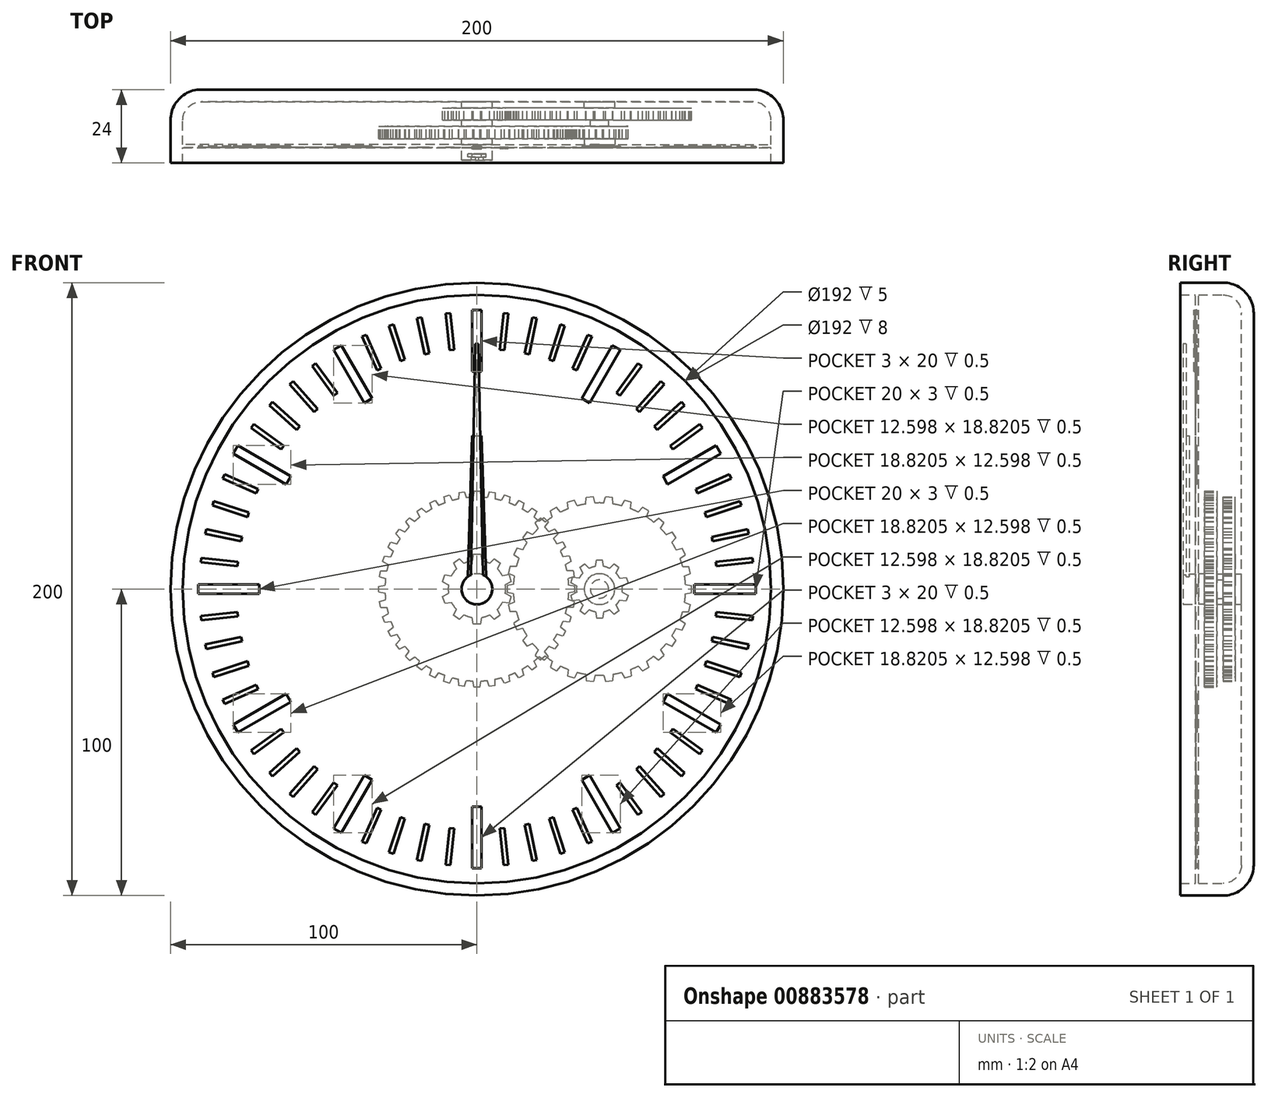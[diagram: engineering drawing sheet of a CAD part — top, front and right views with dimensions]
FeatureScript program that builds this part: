
annotation { "Feature Type Name" : "Feature", "Feature Type Description" : "" }
export const myFeature = defineFeature(function(context is Context, id is Id, definition is map)
    precondition{}
    {
        {
            var Q0;
            Q0=qCreatedBy(makeId("Front.planeOp"),FACE);
            var sketch = newSketch(context, id + "F0", { "sketchPlane" : qUnion([Q0])});
            skCircle(sketch, "E0", {"center": v(0, 0) * mm, "radius": 100 * mm});
            skSolve(sketch);
        }
        {
            var Q0;
            Q0 = qSketchRegion(id + "F0", true);
            extrude(context, id + "F1", {"entities" : qUnion([Q0]), "depth" : 24 * mm, "offsetDistance" : 25 * mm});
        }
        {
            var Q0;
            Q0=makeQuery(id+"F1.opExtrude","CAP_EDGE",EDGE,{"disambiguationData":[OSD([sQuery(id+"F0.wireOp",EDGE,"E0")])],"isStart":true});
            fillet(context, id + "F2", {"entities" : qUnion([Q0]), "radius" : 10 * mm, "tangentPropagation" : true, "allowEdgeOverflow" : false});
        }
        {
            var Q0;
            Q0=makeQuery(id+"F1.opExtrude","CAP_FACE",FACE,{"disambiguationData":[OSD([sQuery(id+"F0.wireOp",EDGE,"E0")])],"isStart":false});
            shell(context, id + "F3", {"entities" : qUnion([Q0]), "thickness" : 4 * mm});
        }
        {
            var Q0;
            {var subQ0=sQuery(id+"F0.wireOp",EDGE,"E0");Q0=makeQuery(id+"F3.opShell","OFFSET_FACE",FACE,{"disambiguationData":[OSD([subQ0]),TDD([makeQuery(id+"F1.opExtrude","CAP_FACE",FACE,{"disambiguationData":[OSD([subQ0])],"isStart":true})])]});}
            var sketch = newSketch(context, id + "F4", { "sketchPlane" : qUnion([Q0])});
            skCircle(sketch, "E1", {"center": v(0, 0) * mm, "radius": 5 * mm});
            skCircle(sketch, "E2", {"center": v(0, 0) * mm, "radius": 3 * mm});
            skCircle(sketch, "E3", {"center": v(40, 0) * mm, "radius": 5 * mm});
            skCircle(sketch, "E4", {"center": v(40, 0) * mm, "radius": 3 * mm});
            skSolve(sketch);
        }
        {
            var Q0;
            Q0 = qSketchRegion(id + "F4", true);
            extrude(context, id + "F5", {"entities" : qUnion([Q0]), "operationType" : NewBodyOperationType.ADD, "depth" : 2 * mm, "offsetDistance" : 25 * mm});
        }
        {
            var Q0;
            {var subQ0=sQuery(id+"F0.wireOp",EDGE,"E0");Q0=makeQuery(id+"F5.boolean.opBoolean","SPLIT",FACE,{"disambiguationData":[TD([makeQuery(id+"F5.opExtrude","SWEPT_FACE",FACE,{"disambiguationData":[OSD([sQuery(id+"F4.wireOp",EDGE,"E2")])]})])],"derivedFrom":makeQuery(id+"F3.opShell","OFFSET_FACE",FACE,{"disambiguationData":[OSD([subQ0]),TDD([makeQuery(id+"F1.opExtrude","CAP_FACE",FACE,{"disambiguationData":[OSD([subQ0])],"isStart":true})])]})});}
            extrude(context, id + "F6", {"entities" : qUnion([Q0]), "depth" : 19 * mm, "offsetDistance" : 25 * mm});
        }
        {
            var Q0;
            {var subQ0=sQuery(id+"F0.wireOp",EDGE,"E0");Q0=makeQuery(id+"F5.boolean.opBoolean","SPLIT",FACE,{"disambiguationData":[TD([makeQuery(id+"F5.opExtrude","SWEPT_FACE",FACE,{"disambiguationData":[OSD([sQuery(id+"F4.wireOp",EDGE,"E4")])]})])],"derivedFrom":makeQuery(id+"F3.opShell","OFFSET_FACE",FACE,{"disambiguationData":[OSD([subQ0]),TDD([makeQuery(id+"F1.opExtrude","CAP_FACE",FACE,{"disambiguationData":[OSD([subQ0])],"isStart":true})])]})});}
            extrude(context, id + "F7", {"entities" : qUnion([Q0]), "depth" : 8 * mm, "offsetDistance" : 25 * mm});
        }
        {
            var Q0;
            Q0=makeQuery(id+"F5.opExtrude","CAP_FACE",FACE,{"disambiguationData":[OSD([sQuery(id+"F4.wireOp",EDGE,"E1"),sQuery(id+"F4.wireOp",EDGE,"E2")])],"isStart":false});
            var sketch = newSketch(context, id + "F8", { "sketchPlane" : qUnion([Q0])});
            skCircle(sketch, "E5", {"center": v(0, 0) * mm, "radius": 9.38 * mm});
            skLineSegment(sketch, "E6", {"start": v(0, 11.38) * mm, "end": v(1.18, 11.38) * mm});
            skLineSegment(sketch, "E7", {"start": v(1.18, 11.38) * mm, "end": v(1.55, 9.25) * mm});
            skLineSegment(sketch, "E8.MirrorCS", {"start": v(0, 11.38) * mm, "end": v(-1.18, 11.38) * mm});
            skLineSegment(sketch, "E9.MirrorCS", {"start": v(-1.18, 11.38) * mm, "end": v(-1.55, 9.25) * mm});
            skLineSegment(sketch, "E10.1.0", {"start": v(-6.69, 9.2) * mm, "end": v(-5.73, 9.9) * mm});
            skLineSegment(sketch, "E10.1.1", {"start": v(-6.69, 9.2) * mm, "end": v(-7.64, 8.51) * mm});
            skLineSegment(sketch, "E10.1.2", {"start": v(-5.73, 9.9) * mm, "end": v(-4.18, 8.4) * mm});
            skLineSegment(sketch, "E10.1.3", {"start": v(-7.64, 8.51) * mm, "end": v(-6.7, 6.57) * mm});
            skLineSegment(sketch, "E10.2.0", {"start": v(-10.82, 3.52) * mm, "end": v(-10.45, 4.64) * mm});
            skLineSegment(sketch, "E10.2.1", {"start": v(-10.82, 3.52) * mm, "end": v(-11.18, 2.4) * mm});
            skLineSegment(sketch, "E10.2.2", {"start": v(-10.45, 4.64) * mm, "end": v(-8.31, 4.33) * mm});
            skLineSegment(sketch, "E10.2.3", {"start": v(-11.18, 2.4) * mm, "end": v(-9.27, 1.38) * mm});
            skLineSegment(sketch, "E11.3.3.0", {"start": v(-10.82, -3.52) * mm, "end": v(-10.45, -4.64) * mm});
            skLineSegment(sketch, "E11.6.3.0", {"start": v(-11.18, -2.4) * mm, "end": v(-9.27, -1.38) * mm});
            skLineSegment(sketch, "E11.8.3.0", {"start": v(-10.82, -3.52) * mm, "end": v(-11.18, -2.4) * mm});
            skLineSegment(sketch, "E11.9.3.0", {"start": v(-10.45, -4.64) * mm, "end": v(-8.31, -4.33) * mm});
            skLineSegment(sketch, "E11.3.4.0", {"start": v(-6.69, -9.2) * mm, "end": v(-5.73, -9.9) * mm});
            skLineSegment(sketch, "E11.6.4.0", {"start": v(-7.64, -8.51) * mm, "end": v(-6.7, -6.57) * mm});
            skLineSegment(sketch, "E11.8.4.0", {"start": v(-6.69, -9.2) * mm, "end": v(-7.64, -8.51) * mm});
            skLineSegment(sketch, "E11.9.4.0", {"start": v(-5.73, -9.9) * mm, "end": v(-4.18, -8.4) * mm});
            skLineSegment(sketch, "E11.3.5.0", {"start": v(0, -11.38) * mm, "end": v(1.18, -11.38) * mm});
            skLineSegment(sketch, "E11.6.5.0", {"start": v(-1.18, -11.38) * mm, "end": v(-1.55, -9.25) * mm});
            skLineSegment(sketch, "E11.8.5.0", {"start": v(0, -11.38) * mm, "end": v(-1.18, -11.38) * mm});
            skLineSegment(sketch, "E11.9.5.0", {"start": v(1.18, -11.38) * mm, "end": v(1.55, -9.25) * mm});
            skLineSegment(sketch, "E11.3.6.0", {"start": v(6.69, -9.2) * mm, "end": v(7.64, -8.51) * mm});
            skLineSegment(sketch, "E11.6.6.0", {"start": v(5.73, -9.9) * mm, "end": v(4.18, -8.4) * mm});
            skLineSegment(sketch, "E11.8.6.0", {"start": v(6.69, -9.2) * mm, "end": v(5.73, -9.9) * mm});
            skLineSegment(sketch, "E11.9.6.0", {"start": v(7.64, -8.51) * mm, "end": v(6.7, -6.57) * mm});
            skLineSegment(sketch, "E11.3.7.0", {"start": v(10.82, -3.52) * mm, "end": v(11.18, -2.4) * mm});
            skLineSegment(sketch, "E11.6.7.0", {"start": v(10.45, -4.64) * mm, "end": v(8.31, -4.33) * mm});
            skLineSegment(sketch, "E11.8.7.0", {"start": v(10.82, -3.52) * mm, "end": v(10.45, -4.64) * mm});
            skLineSegment(sketch, "E11.9.7.0", {"start": v(11.18, -2.4) * mm, "end": v(9.27, -1.38) * mm});
            skLineSegment(sketch, "E11.3.8.0", {"start": v(10.82, 3.52) * mm, "end": v(10.45, 4.64) * mm});
            skLineSegment(sketch, "E11.6.8.0", {"start": v(11.18, 2.4) * mm, "end": v(9.27, 1.38) * mm});
            skLineSegment(sketch, "E11.8.8.0", {"start": v(10.82, 3.52) * mm, "end": v(11.18, 2.4) * mm});
            skLineSegment(sketch, "E11.9.8.0", {"start": v(10.45, 4.64) * mm, "end": v(8.31, 4.33) * mm});
            skLineSegment(sketch, "E11.3.9.0", {"start": v(6.69, 9.2) * mm, "end": v(5.73, 9.9) * mm});
            skLineSegment(sketch, "E11.6.9.0", {"start": v(7.64, 8.51) * mm, "end": v(6.7, 6.57) * mm});
            skLineSegment(sketch, "E11.8.9.0", {"start": v(6.69, 9.2) * mm, "end": v(7.64, 8.51) * mm});
            skLineSegment(sketch, "E11.9.9.0", {"start": v(5.73, 9.9) * mm, "end": v(4.18, 8.4) * mm});
            skSolve(sketch);
        }
        {
            var Q0;
            Q0 = qSketchRegion(id + "F8", true);
            extrude(context, id + "F9", {"entities" : qUnion([Q0]), "operationType" : NewBodyOperationType.ADD, "depth" : 4 * mm, "offsetDistance" : 25 * mm});
        }
        {
            var Q0;
            Q0=makeQuery(id+"F5.opExtrude","CAP_FACE",FACE,{"disambiguationData":[OSD([sQuery(id+"F4.wireOp",EDGE,"E3"),sQuery(id+"F4.wireOp",EDGE,"E4")])],"isStart":false});
            var sketch = newSketch(context, id + "F10", { "sketchPlane" : qUnion([Q0])});
            skCircle(sketch, "E12", {"center": v(40, 0) * mm, "radius": 28.12 * mm});
            skLineSegment(sketch, "E13", {"start": v(11.92, 1.53) * mm, "end": v(9.9, 1.18) * mm});
            skLineSegment(sketch, "E14", {"start": v(9.9, 1.18) * mm, "end": v(9.9, 0) * mm});
            skLineSegment(sketch, "E15.MirrorCS", {"start": v(9.9, -1.18) * mm, "end": v(9.9, 0) * mm});
            skLineSegment(sketch, "E16.MirrorCS", {"start": v(11.92, -1.53) * mm, "end": v(9.9, -1.18) * mm});
            skLineSegment(sketch, "E17.1.0", {"start": v(12.21, -4.34) * mm, "end": v(10.31, -5.1) * mm});
            skLineSegment(sketch, "E17.1.1", {"start": v(10.31, -5.1) * mm, "end": v(10.56, -6.26) * mm});
            skLineSegment(sketch, "E17.1.2", {"start": v(10.8, -7.41) * mm, "end": v(10.56, -6.26) * mm});
            skLineSegment(sketch, "E17.1.3", {"start": v(12.85, -7.34) * mm, "end": v(10.8, -7.41) * mm});
            skLineSegment(sketch, "E17.2.0", {"start": v(13.72, -10.02) * mm, "end": v(12.02, -11.17) * mm});
            skLineSegment(sketch, "E17.2.1", {"start": v(12.02, -11.17) * mm, "end": v(12.5, -12.24) * mm});
            skLineSegment(sketch, "E17.2.2", {"start": v(12.98, -13.32) * mm, "end": v(12.5, -12.24) * mm});
            skLineSegment(sketch, "E17.2.3", {"start": v(14.97, -12.82) * mm, "end": v(12.98, -13.32) * mm});
            skLineSegment(sketch, "E18.2.3.0", {"start": v(16.38, -15.27) * mm, "end": v(14.95, -16.74) * mm});
            skLineSegment(sketch, "E18.3.3.0", {"start": v(14.95, -16.74) * mm, "end": v(15.65, -17.7) * mm});
            skLineSegment(sketch, "E18.6.3.0", {"start": v(16.34, -18.65) * mm, "end": v(15.65, -17.7) * mm});
            skLineSegment(sketch, "E18.9.3.0", {"start": v(18.18, -17.75) * mm, "end": v(16.34, -18.65) * mm});
            skLineSegment(sketch, "E18.2.4.0", {"start": v(20.07, -19.84) * mm, "end": v(18.98, -21.58) * mm});
            skLineSegment(sketch, "E18.3.4.0", {"start": v(18.98, -21.58) * mm, "end": v(19.86, -22.37) * mm});
            skLineSegment(sketch, "E18.6.4.0", {"start": v(20.73, -23.16) * mm, "end": v(19.86, -22.37) * mm});
            skLineSegment(sketch, "E18.9.4.0", {"start": v(22.35, -21.9) * mm, "end": v(20.73, -23.16) * mm});
            skLineSegment(sketch, "E18.2.5.0", {"start": v(24.63, -23.55) * mm, "end": v(23.93, -25.48) * mm});
            skLineSegment(sketch, "E18.3.5.0", {"start": v(23.93, -25.48) * mm, "end": v(24.95, -26.07) * mm});
            skLineSegment(sketch, "E18.6.5.0", {"start": v(25.97, -26.66) * mm, "end": v(24.95, -26.07) * mm});
            skLineSegment(sketch, "E18.9.5.0", {"start": v(27.29, -25.09) * mm, "end": v(25.97, -26.66) * mm});
            skLineSegment(sketch, "E18.2.6.0", {"start": v(29.86, -26.23) * mm, "end": v(29.58, -28.26) * mm});
            skLineSegment(sketch, "E18.3.6.0", {"start": v(29.58, -28.26) * mm, "end": v(30.7, -28.63) * mm});
            skLineSegment(sketch, "E18.6.6.0", {"start": v(31.82, -29) * mm, "end": v(30.7, -28.63) * mm});
            skLineSegment(sketch, "E18.9.6.0", {"start": v(32.78, -27.18) * mm, "end": v(31.82, -29) * mm});
            skLineSegment(sketch, "E18.2.7.0", {"start": v(35.54, -27.77) * mm, "end": v(35.68, -29.81) * mm});
            skLineSegment(sketch, "E18.3.7.0", {"start": v(35.68, -29.81) * mm, "end": v(36.85, -29.94) * mm});
            skLineSegment(sketch, "E18.6.7.0", {"start": v(38.03, -30.06) * mm, "end": v(36.85, -29.94) * mm});
            skLineSegment(sketch, "E18.9.7.0", {"start": v(38.6, -28.09) * mm, "end": v(38.03, -30.06) * mm});
            skLineSegment(sketch, "E18.2.8.0", {"start": v(41.4, -28.09) * mm, "end": v(41.97, -30.06) * mm});
            skLineSegment(sketch, "E18.3.8.0", {"start": v(41.97, -30.06) * mm, "end": v(43.15, -29.94) * mm});
            skLineSegment(sketch, "E18.6.8.0", {"start": v(44.32, -29.81) * mm, "end": v(43.15, -29.94) * mm});
            skLineSegment(sketch, "E18.9.8.0", {"start": v(44.46, -27.77) * mm, "end": v(44.32, -29.81) * mm});
            skLineSegment(sketch, "E18.2.9.0", {"start": v(47.22, -27.18) * mm, "end": v(48.18, -29) * mm});
            skLineSegment(sketch, "E18.3.9.0", {"start": v(48.18, -29) * mm, "end": v(49.3, -28.63) * mm});
            skLineSegment(sketch, "E18.6.9.0", {"start": v(50.42, -28.26) * mm, "end": v(49.3, -28.63) * mm});
            skLineSegment(sketch, "E18.9.9.0", {"start": v(50.14, -26.23) * mm, "end": v(50.42, -28.26) * mm});
            skLineSegment(sketch, "E19.2.10.0", {"start": v(52.71, -25.09) * mm, "end": v(54.03, -26.66) * mm});
            skLineSegment(sketch, "E19.3.10.0", {"start": v(54.03, -26.66) * mm, "end": v(55.05, -26.07) * mm});
            skLineSegment(sketch, "E19.6.10.0", {"start": v(56.07, -25.48) * mm, "end": v(55.05, -26.07) * mm});
            skLineSegment(sketch, "E19.9.10.0", {"start": v(55.37, -23.55) * mm, "end": v(56.07, -25.48) * mm});
            skLineSegment(sketch, "E19.2.11.0", {"start": v(57.65, -21.9) * mm, "end": v(59.27, -23.16) * mm});
            skLineSegment(sketch, "E19.3.11.0", {"start": v(59.27, -23.16) * mm, "end": v(60.14, -22.37) * mm});
            skLineSegment(sketch, "E19.6.11.0", {"start": v(61.02, -21.58) * mm, "end": v(60.14, -22.37) * mm});
            skLineSegment(sketch, "E19.9.11.0", {"start": v(59.93, -19.84) * mm, "end": v(61.02, -21.58) * mm});
            skLineSegment(sketch, "E19.2.12.0", {"start": v(61.82, -17.75) * mm, "end": v(63.66, -18.65) * mm});
            skLineSegment(sketch, "E19.3.12.0", {"start": v(63.66, -18.65) * mm, "end": v(64.35, -17.7) * mm});
            skLineSegment(sketch, "E19.6.12.0", {"start": v(65.05, -16.74) * mm, "end": v(64.35, -17.7) * mm});
            skLineSegment(sketch, "E19.9.12.0", {"start": v(63.62, -15.27) * mm, "end": v(65.05, -16.74) * mm});
            skLineSegment(sketch, "E19.2.13.0", {"start": v(65.03, -12.82) * mm, "end": v(67.02, -13.32) * mm});
            skLineSegment(sketch, "E19.3.13.0", {"start": v(67.02, -13.32) * mm, "end": v(67.5, -12.24) * mm});
            skLineSegment(sketch, "E19.6.13.0", {"start": v(67.98, -11.17) * mm, "end": v(67.5, -12.24) * mm});
            skLineSegment(sketch, "E19.9.13.0", {"start": v(66.28, -10.02) * mm, "end": v(67.98, -11.17) * mm});
            skLineSegment(sketch, "E19.2.14.0", {"start": v(67.15, -7.34) * mm, "end": v(69.2, -7.41) * mm});
            skLineSegment(sketch, "E19.3.14.0", {"start": v(69.2, -7.41) * mm, "end": v(69.44, -6.26) * mm});
            skLineSegment(sketch, "E19.6.14.0", {"start": v(69.69, -5.1) * mm, "end": v(69.44, -6.26) * mm});
            skLineSegment(sketch, "E19.9.14.0", {"start": v(67.79, -4.34) * mm, "end": v(69.69, -5.1) * mm});
            skLineSegment(sketch, "E19.2.15.0", {"start": v(68.08, -1.53) * mm, "end": v(70.1, -1.18) * mm});
            skLineSegment(sketch, "E19.3.15.0", {"start": v(70.1, -1.18) * mm, "end": v(70.1, 0) * mm});
            skLineSegment(sketch, "E19.6.15.0", {"start": v(70.1, 1.18) * mm, "end": v(70.1, 0) * mm});
            skLineSegment(sketch, "E19.9.15.0", {"start": v(68.08, 1.53) * mm, "end": v(70.1, 1.18) * mm});
            skLineSegment(sketch, "E19.2.16.0", {"start": v(67.79, 4.34) * mm, "end": v(69.69, 5.1) * mm});
            skLineSegment(sketch, "E19.3.16.0", {"start": v(69.69, 5.1) * mm, "end": v(69.44, 6.26) * mm});
            skLineSegment(sketch, "E19.6.16.0", {"start": v(69.2, 7.41) * mm, "end": v(69.44, 6.26) * mm});
            skLineSegment(sketch, "E19.9.16.0", {"start": v(67.15, 7.34) * mm, "end": v(69.2, 7.41) * mm});
            skLineSegment(sketch, "E19.2.17.0", {"start": v(66.28, 10.02) * mm, "end": v(67.98, 11.17) * mm});
            skLineSegment(sketch, "E19.3.17.0", {"start": v(67.98, 11.17) * mm, "end": v(67.5, 12.24) * mm});
            skLineSegment(sketch, "E19.6.17.0", {"start": v(67.02, 13.32) * mm, "end": v(67.5, 12.24) * mm});
            skLineSegment(sketch, "E19.9.17.0", {"start": v(65.03, 12.82) * mm, "end": v(67.02, 13.32) * mm});
            skLineSegment(sketch, "E19.2.18.0", {"start": v(63.62, 15.27) * mm, "end": v(65.05, 16.74) * mm});
            skLineSegment(sketch, "E19.3.18.0", {"start": v(65.05, 16.74) * mm, "end": v(64.35, 17.7) * mm});
            skLineSegment(sketch, "E19.6.18.0", {"start": v(63.66, 18.65) * mm, "end": v(64.35, 17.7) * mm});
            skLineSegment(sketch, "E19.9.18.0", {"start": v(61.82, 17.75) * mm, "end": v(63.66, 18.65) * mm});
            skLineSegment(sketch, "E19.2.19.0", {"start": v(59.93, 19.84) * mm, "end": v(61.02, 21.58) * mm});
            skLineSegment(sketch, "E19.3.19.0", {"start": v(61.02, 21.58) * mm, "end": v(60.14, 22.37) * mm});
            skLineSegment(sketch, "E19.6.19.0", {"start": v(59.27, 23.16) * mm, "end": v(60.14, 22.37) * mm});
            skLineSegment(sketch, "E19.9.19.0", {"start": v(57.65, 21.9) * mm, "end": v(59.27, 23.16) * mm});
            skLineSegment(sketch, "E19.2.20.0", {"start": v(55.37, 23.55) * mm, "end": v(56.07, 25.48) * mm});
            skLineSegment(sketch, "E19.3.20.0", {"start": v(56.07, 25.48) * mm, "end": v(55.05, 26.07) * mm});
            skLineSegment(sketch, "E19.6.20.0", {"start": v(54.03, 26.66) * mm, "end": v(55.05, 26.07) * mm});
            skLineSegment(sketch, "E19.9.20.0", {"start": v(52.71, 25.09) * mm, "end": v(54.03, 26.66) * mm});
            skLineSegment(sketch, "E19.2.21.0", {"start": v(50.14, 26.23) * mm, "end": v(50.42, 28.26) * mm});
            skLineSegment(sketch, "E19.3.21.0", {"start": v(50.42, 28.26) * mm, "end": v(49.3, 28.63) * mm});
            skLineSegment(sketch, "E19.6.21.0", {"start": v(48.18, 29) * mm, "end": v(49.3, 28.63) * mm});
            skLineSegment(sketch, "E19.9.21.0", {"start": v(47.22, 27.18) * mm, "end": v(48.18, 29) * mm});
            skLineSegment(sketch, "E19.2.22.0", {"start": v(44.46, 27.77) * mm, "end": v(44.32, 29.81) * mm});
            skLineSegment(sketch, "E19.3.22.0", {"start": v(44.32, 29.81) * mm, "end": v(43.15, 29.94) * mm});
            skLineSegment(sketch, "E19.6.22.0", {"start": v(41.97, 30.06) * mm, "end": v(43.15, 29.94) * mm});
            skLineSegment(sketch, "E19.9.22.0", {"start": v(41.4, 28.09) * mm, "end": v(41.97, 30.06) * mm});
            skLineSegment(sketch, "E19.2.23.0", {"start": v(38.6, 28.09) * mm, "end": v(38.03, 30.06) * mm});
            skLineSegment(sketch, "E19.3.23.0", {"start": v(38.03, 30.06) * mm, "end": v(36.85, 29.94) * mm});
            skLineSegment(sketch, "E19.6.23.0", {"start": v(35.68, 29.81) * mm, "end": v(36.85, 29.94) * mm});
            skLineSegment(sketch, "E19.9.23.0", {"start": v(35.54, 27.77) * mm, "end": v(35.68, 29.81) * mm});
            skLineSegment(sketch, "E19.2.24.0", {"start": v(32.78, 27.18) * mm, "end": v(31.82, 29) * mm});
            skLineSegment(sketch, "E19.3.24.0", {"start": v(31.82, 29) * mm, "end": v(30.7, 28.63) * mm});
            skLineSegment(sketch, "E19.6.24.0", {"start": v(29.58, 28.26) * mm, "end": v(30.7, 28.63) * mm});
            skLineSegment(sketch, "E19.9.24.0", {"start": v(29.86, 26.23) * mm, "end": v(29.58, 28.26) * mm});
            skLineSegment(sketch, "E19.2.25.0", {"start": v(27.29, 25.09) * mm, "end": v(25.97, 26.66) * mm});
            skLineSegment(sketch, "E19.3.25.0", {"start": v(25.97, 26.66) * mm, "end": v(24.95, 26.07) * mm});
            skLineSegment(sketch, "E19.6.25.0", {"start": v(23.93, 25.48) * mm, "end": v(24.95, 26.07) * mm});
            skLineSegment(sketch, "E19.9.25.0", {"start": v(24.63, 23.55) * mm, "end": v(23.93, 25.48) * mm});
            skLineSegment(sketch, "E19.2.26.0", {"start": v(22.35, 21.9) * mm, "end": v(20.73, 23.16) * mm});
            skLineSegment(sketch, "E19.3.26.0", {"start": v(20.73, 23.16) * mm, "end": v(19.86, 22.37) * mm});
            skLineSegment(sketch, "E19.6.26.0", {"start": v(18.98, 21.58) * mm, "end": v(19.86, 22.37) * mm});
            skLineSegment(sketch, "E19.9.26.0", {"start": v(20.07, 19.84) * mm, "end": v(18.98, 21.58) * mm});
            skLineSegment(sketch, "E19.2.27.0", {"start": v(18.18, 17.75) * mm, "end": v(16.34, 18.65) * mm});
            skLineSegment(sketch, "E19.3.27.0", {"start": v(16.34, 18.65) * mm, "end": v(15.65, 17.7) * mm});
            skLineSegment(sketch, "E19.6.27.0", {"start": v(14.95, 16.74) * mm, "end": v(15.65, 17.7) * mm});
            skLineSegment(sketch, "E19.9.27.0", {"start": v(16.38, 15.27) * mm, "end": v(14.95, 16.74) * mm});
            skLineSegment(sketch, "E19.2.28.0", {"start": v(14.97, 12.82) * mm, "end": v(12.98, 13.32) * mm});
            skLineSegment(sketch, "E19.3.28.0", {"start": v(12.98, 13.32) * mm, "end": v(12.5, 12.24) * mm});
            skLineSegment(sketch, "E19.6.28.0", {"start": v(12.02, 11.17) * mm, "end": v(12.5, 12.24) * mm});
            skLineSegment(sketch, "E19.9.28.0", {"start": v(13.72, 10.02) * mm, "end": v(12.02, 11.17) * mm});
            skLineSegment(sketch, "E19.2.29.0", {"start": v(12.85, 7.34) * mm, "end": v(10.8, 7.41) * mm});
            skLineSegment(sketch, "E19.3.29.0", {"start": v(10.8, 7.41) * mm, "end": v(10.56, 6.26) * mm});
            skLineSegment(sketch, "E19.6.29.0", {"start": v(10.31, 5.1) * mm, "end": v(10.56, 6.26) * mm});
            skLineSegment(sketch, "E19.9.29.0", {"start": v(12.21, 4.34) * mm, "end": v(10.31, 5.1) * mm});
            skSolve(sketch);
        }
        {
            var Q0;
            Q0 = qSketchRegion(id + "F10", true);
            extrude(context, id + "F11", {"entities" : qUnion([Q0]), "operationType" : NewBodyOperationType.ADD, "depth" : 4 * mm, "offsetDistance" : 25 * mm});
        }
        {
            var Q0;
            Q0=makeQuery(id+"F9.opExtrude","CAP_FACE",FACE,{"disambiguationData":[OSD([sQuery(id+"F8.wireOp",EDGE,"E5"),sQuery(id+"F8.wireOp",EDGE,"E6"),sQuery(id+"F8.wireOp",EDGE,"E7"),sQuery(id+"F8.wireOp",EDGE,"E8.MirrorCS"),sQuery(id+"F8.wireOp",EDGE,"E9.MirrorCS"),sQuery(id+"F8.wireOp",EDGE,"E10.1.0"),sQuery(id+"F8.wireOp",EDGE,"E10.1.1"),sQuery(id+"F8.wireOp",EDGE,"E10.1.2"),sQuery(id+"F8.wireOp",EDGE,"E10.1.3"),sQuery(id+"F8.wireOp",EDGE,"E10.2.0"),sQuery(id+"F8.wireOp",EDGE,"E10.2.1"),sQuery(id+"F8.wireOp",EDGE,"E10.2.2"),sQuery(id+"F8.wireOp",EDGE,"E10.2.3"),sQuery(id+"F8.wireOp",EDGE,"E11.3.3.0"),sQuery(id+"F8.wireOp",EDGE,"E11.6.3.0"),sQuery(id+"F8.wireOp",EDGE,"E11.8.3.0"),sQuery(id+"F8.wireOp",EDGE,"E11.9.3.0"),sQuery(id+"F8.wireOp",EDGE,"E11.3.4.0"),sQuery(id+"F8.wireOp",EDGE,"E11.6.4.0"),sQuery(id+"F8.wireOp",EDGE,"E11.8.4.0"),sQuery(id+"F8.wireOp",EDGE,"E11.9.4.0"),sQuery(id+"F8.wireOp",EDGE,"E11.3.5.0"),sQuery(id+"F8.wireOp",EDGE,"E11.6.5.0"),sQuery(id+"F8.wireOp",EDGE,"E11.8.5.0"),sQuery(id+"F8.wireOp",EDGE,"E11.9.5.0"),sQuery(id+"F8.wireOp",EDGE,"E11.3.6.0"),sQuery(id+"F8.wireOp",EDGE,"E11.6.6.0"),sQuery(id+"F8.wireOp",EDGE,"E11.8.6.0"),sQuery(id+"F8.wireOp",EDGE,"E11.9.6.0"),sQuery(id+"F8.wireOp",EDGE,"E11.3.7.0"),sQuery(id+"F8.wireOp",EDGE,"E11.6.7.0"),sQuery(id+"F8.wireOp",EDGE,"E11.8.7.0"),sQuery(id+"F8.wireOp",EDGE,"E11.9.7.0"),sQuery(id+"F8.wireOp",EDGE,"E11.3.8.0"),sQuery(id+"F8.wireOp",EDGE,"E11.6.8.0"),sQuery(id+"F8.wireOp",EDGE,"E11.8.8.0"),sQuery(id+"F8.wireOp",EDGE,"E11.9.8.0"),sQuery(id+"F8.wireOp",EDGE,"E11.3.9.0"),sQuery(id+"F8.wireOp",EDGE,"E11.6.9.0"),sQuery(id+"F8.wireOp",EDGE,"E11.8.9.0"),sQuery(id+"F8.wireOp",EDGE,"E11.9.9.0")])],"isStart":false});
            var sketch = newSketch(context, id + "F12", { "sketchPlane" : qUnion([Q0])});
            skCircle(sketch, "E20.0", {"center": v(0, 0) * mm, "radius": 3 * mm});
            skCircle(sketch, "E21.0", {"center": v(0, 0) * mm, "radius": 5 * mm});
            skSolve(sketch);
        }
        {
            var Q0;
            Q0 = qSketchRegion(id + "F12", true);
            extrude(context, id + "F13", {"entities" : qUnion([Q0]), "depth" : 2 * mm, "offsetDistance" : 25 * mm});
        }
        {
            var Q0;
            Q0=makeQuery(id+"F13.opExtrude","CAP_FACE",FACE,{"disambiguationData":[OSD([sQuery(id+"F12.wireOp",EDGE,"E20.0"),sQuery(id+"F12.wireOp",EDGE,"E21.0")])],"isStart":false});
            var sketch = newSketch(context, id + "F14", { "sketchPlane" : qUnion([Q0])});
            skCircle(sketch, "E22.0.0", {"center": v(0, 0) * mm, "radius": 3 * mm});
            skCircle(sketch, "E23", {"center": v(0, 0) * mm, "radius": 30 * mm});
            skLineSegment(sketch, "E24", {"start": v(0, 32) * mm, "end": v(0.94, 32) * mm});
            skLineSegment(sketch, "E25", {"start": v(0.94, 32) * mm, "end": v(1.3, 29.97) * mm});
            skLineSegment(sketch, "E26.MirrorCS", {"start": v(0, 32) * mm, "end": v(-0.94, 32) * mm});
            skLineSegment(sketch, "E27.MirrorCS", {"start": v(-0.94, 32) * mm, "end": v(-1.3, 29.97) * mm});
            skLineSegment(sketch, "E28.1.0", {"start": v(-5, 31.6) * mm, "end": v(-4.08, 31.75) * mm});
            skLineSegment(sketch, "E28.1.1", {"start": v(-5, 31.6) * mm, "end": v(-5.94, 31.46) * mm});
            skLineSegment(sketch, "E28.1.2", {"start": v(-4.08, 31.75) * mm, "end": v(-3.4, 29.8) * mm});
            skLineSegment(sketch, "E28.1.3", {"start": v(-5.94, 31.46) * mm, "end": v(-5.97, 29.4) * mm});
            skLineSegment(sketch, "E28.2.0", {"start": v(-9.89, 30.43) * mm, "end": v(-9, 30.73) * mm});
            skLineSegment(sketch, "E28.2.1", {"start": v(-9.89, 30.43) * mm, "end": v(-10.78, 30.14) * mm});
            skLineSegment(sketch, "E28.2.2", {"start": v(-9, 30.73) * mm, "end": v(-8.03, 28.9) * mm});
            skLineSegment(sketch, "E28.2.3", {"start": v(-10.78, 30.14) * mm, "end": v(-10.5, 28.1) * mm});
            skLineSegment(sketch, "E29.1.3.0", {"start": v(-14.53, 28.51) * mm, "end": v(-13.69, 28.94) * mm});
            skLineSegment(sketch, "E29.3.3.0", {"start": v(-14.53, 28.51) * mm, "end": v(-15.37, 28.08) * mm});
            skLineSegment(sketch, "E29.6.3.0", {"start": v(-13.69, 28.94) * mm, "end": v(-12.45, 27.3) * mm});
            skLineSegment(sketch, "E29.9.3.0", {"start": v(-15.37, 28.08) * mm, "end": v(-14.77, 26.11) * mm});
            skLineSegment(sketch, "E29.1.4.0", {"start": v(-18.8, 25.89) * mm, "end": v(-18.05, 26.44) * mm});
            skLineSegment(sketch, "E29.3.4.0", {"start": v(-18.8, 25.89) * mm, "end": v(-19.57, 25.33) * mm});
            skLineSegment(sketch, "E29.6.4.0", {"start": v(-18.05, 26.44) * mm, "end": v(-16.57, 25.01) * mm});
            skLineSegment(sketch, "E29.9.4.0", {"start": v(-19.57, 25.33) * mm, "end": v(-18.67, 23.48) * mm});
            skLineSegment(sketch, "E29.1.5.0", {"start": v(-22.63, 22.63) * mm, "end": v(-21.96, 23.3) * mm});
            skLineSegment(sketch, "E29.3.5.0", {"start": v(-22.63, 22.63) * mm, "end": v(-23.3, 21.96) * mm});
            skLineSegment(sketch, "E29.6.5.0", {"start": v(-21.96, 23.3) * mm, "end": v(-20.27, 22.11) * mm});
            skLineSegment(sketch, "E29.9.5.0", {"start": v(-23.3, 21.96) * mm, "end": v(-22.11, 20.27) * mm});
            skLineSegment(sketch, "E29.1.6.0", {"start": v(-25.89, 18.8) * mm, "end": v(-25.33, 19.57) * mm});
            skLineSegment(sketch, "E29.3.6.0", {"start": v(-25.89, 18.8) * mm, "end": v(-26.44, 18.05) * mm});
            skLineSegment(sketch, "E29.6.6.0", {"start": v(-25.33, 19.57) * mm, "end": v(-23.48, 18.67) * mm});
            skLineSegment(sketch, "E29.9.6.0", {"start": v(-26.44, 18.05) * mm, "end": v(-25.01, 16.57) * mm});
            skLineSegment(sketch, "E29.1.7.0", {"start": v(-28.51, 14.53) * mm, "end": v(-28.08, 15.37) * mm});
            skLineSegment(sketch, "E29.3.7.0", {"start": v(-28.51, 14.53) * mm, "end": v(-28.94, 13.69) * mm});
            skLineSegment(sketch, "E29.6.7.0", {"start": v(-28.08, 15.37) * mm, "end": v(-26.11, 14.77) * mm});
            skLineSegment(sketch, "E29.9.7.0", {"start": v(-28.94, 13.69) * mm, "end": v(-27.3, 12.45) * mm});
            skLineSegment(sketch, "E29.1.8.0", {"start": v(-30.43, 9.89) * mm, "end": v(-30.14, 10.78) * mm});
            skLineSegment(sketch, "E29.3.8.0", {"start": v(-30.43, 9.89) * mm, "end": v(-30.73, 9) * mm});
            skLineSegment(sketch, "E29.6.8.0", {"start": v(-30.14, 10.78) * mm, "end": v(-28.1, 10.5) * mm});
            skLineSegment(sketch, "E29.9.8.0", {"start": v(-30.73, 9) * mm, "end": v(-28.9, 8.03) * mm});
            skLineSegment(sketch, "E29.1.9.0", {"start": v(-31.6, 5) * mm, "end": v(-31.46, 5.94) * mm});
            skLineSegment(sketch, "E29.3.9.0", {"start": v(-31.6, 5) * mm, "end": v(-31.75, 4.08) * mm});
            skLineSegment(sketch, "E29.6.9.0", {"start": v(-31.46, 5.94) * mm, "end": v(-29.4, 5.97) * mm});
            skLineSegment(sketch, "E29.9.9.0", {"start": v(-31.75, 4.08) * mm, "end": v(-29.8, 3.4) * mm});
            skLineSegment(sketch, "E29.1.10.0", {"start": v(-32, 0) * mm, "end": v(-32, 0.94) * mm});
            skLineSegment(sketch, "E29.3.10.0", {"start": v(-32, 0) * mm, "end": v(-32, -0.94) * mm});
            skLineSegment(sketch, "E29.6.10.0", {"start": v(-32, 0.94) * mm, "end": v(-29.97, 1.3) * mm});
            skLineSegment(sketch, "E29.9.10.0", {"start": v(-32, -0.94) * mm, "end": v(-29.97, -1.3) * mm});
            skLineSegment(sketch, "E29.1.11.0", {"start": v(-31.6, -5) * mm, "end": v(-31.75, -4.08) * mm});
            skLineSegment(sketch, "E29.3.11.0", {"start": v(-31.6, -5) * mm, "end": v(-31.46, -5.94) * mm});
            skLineSegment(sketch, "E29.6.11.0", {"start": v(-31.75, -4.08) * mm, "end": v(-29.8, -3.4) * mm});
            skLineSegment(sketch, "E29.9.11.0", {"start": v(-31.46, -5.94) * mm, "end": v(-29.4, -5.97) * mm});
            skLineSegment(sketch, "E29.1.12.0", {"start": v(-30.43, -9.89) * mm, "end": v(-30.73, -9) * mm});
            skLineSegment(sketch, "E29.3.12.0", {"start": v(-30.43, -9.89) * mm, "end": v(-30.14, -10.78) * mm});
            skLineSegment(sketch, "E29.6.12.0", {"start": v(-30.73, -9) * mm, "end": v(-28.9, -8.03) * mm});
            skLineSegment(sketch, "E29.9.12.0", {"start": v(-30.14, -10.78) * mm, "end": v(-28.1, -10.5) * mm});
            skLineSegment(sketch, "E29.1.13.0", {"start": v(-28.51, -14.53) * mm, "end": v(-28.94, -13.69) * mm});
            skLineSegment(sketch, "E29.3.13.0", {"start": v(-28.51, -14.53) * mm, "end": v(-28.08, -15.37) * mm});
            skLineSegment(sketch, "E29.6.13.0", {"start": v(-28.94, -13.69) * mm, "end": v(-27.3, -12.45) * mm});
            skLineSegment(sketch, "E29.9.13.0", {"start": v(-28.08, -15.37) * mm, "end": v(-26.11, -14.77) * mm});
            skLineSegment(sketch, "E29.1.14.0", {"start": v(-25.89, -18.8) * mm, "end": v(-26.44, -18.05) * mm});
            skLineSegment(sketch, "E29.3.14.0", {"start": v(-25.89, -18.8) * mm, "end": v(-25.33, -19.57) * mm});
            skLineSegment(sketch, "E29.6.14.0", {"start": v(-26.44, -18.05) * mm, "end": v(-25.01, -16.57) * mm});
            skLineSegment(sketch, "E29.9.14.0", {"start": v(-25.33, -19.57) * mm, "end": v(-23.48, -18.67) * mm});
            skLineSegment(sketch, "E29.1.15.0", {"start": v(-22.63, -22.63) * mm, "end": v(-23.3, -21.96) * mm});
            skLineSegment(sketch, "E29.3.15.0", {"start": v(-22.63, -22.63) * mm, "end": v(-21.96, -23.3) * mm});
            skLineSegment(sketch, "E29.6.15.0", {"start": v(-23.3, -21.96) * mm, "end": v(-22.11, -20.27) * mm});
            skLineSegment(sketch, "E29.9.15.0", {"start": v(-21.96, -23.3) * mm, "end": v(-20.27, -22.11) * mm});
            skLineSegment(sketch, "E29.1.16.0", {"start": v(-18.8, -25.89) * mm, "end": v(-19.57, -25.33) * mm});
            skLineSegment(sketch, "E29.3.16.0", {"start": v(-18.8, -25.89) * mm, "end": v(-18.05, -26.44) * mm});
            skLineSegment(sketch, "E29.6.16.0", {"start": v(-19.57, -25.33) * mm, "end": v(-18.67, -23.48) * mm});
            skLineSegment(sketch, "E29.9.16.0", {"start": v(-18.05, -26.44) * mm, "end": v(-16.57, -25.01) * mm});
            skLineSegment(sketch, "E29.1.17.0", {"start": v(-14.53, -28.51) * mm, "end": v(-15.37, -28.08) * mm});
            skLineSegment(sketch, "E29.3.17.0", {"start": v(-14.53, -28.51) * mm, "end": v(-13.69, -28.94) * mm});
            skLineSegment(sketch, "E29.6.17.0", {"start": v(-15.37, -28.08) * mm, "end": v(-14.77, -26.11) * mm});
            skLineSegment(sketch, "E29.9.17.0", {"start": v(-13.69, -28.94) * mm, "end": v(-12.45, -27.3) * mm});
            skLineSegment(sketch, "E29.1.18.0", {"start": v(-9.89, -30.43) * mm, "end": v(-10.78, -30.14) * mm});
            skLineSegment(sketch, "E29.3.18.0", {"start": v(-9.89, -30.43) * mm, "end": v(-9, -30.73) * mm});
            skLineSegment(sketch, "E29.6.18.0", {"start": v(-10.78, -30.14) * mm, "end": v(-10.5, -28.1) * mm});
            skLineSegment(sketch, "E29.9.18.0", {"start": v(-9, -30.73) * mm, "end": v(-8.03, -28.9) * mm});
            skLineSegment(sketch, "E29.1.19.0", {"start": v(-5, -31.6) * mm, "end": v(-5.94, -31.46) * mm});
            skLineSegment(sketch, "E29.3.19.0", {"start": v(-5, -31.6) * mm, "end": v(-4.08, -31.75) * mm});
            skLineSegment(sketch, "E29.6.19.0", {"start": v(-5.94, -31.46) * mm, "end": v(-5.97, -29.4) * mm});
            skLineSegment(sketch, "E29.9.19.0", {"start": v(-4.08, -31.75) * mm, "end": v(-3.4, -29.8) * mm});
            skLineSegment(sketch, "E29.1.20.0", {"start": v(0, -32) * mm, "end": v(-0.94, -32) * mm});
            skLineSegment(sketch, "E29.3.20.0", {"start": v(0, -32) * mm, "end": v(0.94, -32) * mm});
            skLineSegment(sketch, "E29.6.20.0", {"start": v(-0.94, -32) * mm, "end": v(-1.3, -29.97) * mm});
            skLineSegment(sketch, "E29.9.20.0", {"start": v(0.94, -32) * mm, "end": v(1.3, -29.97) * mm});
            skLineSegment(sketch, "E29.1.21.0", {"start": v(5, -31.6) * mm, "end": v(4.08, -31.75) * mm});
            skLineSegment(sketch, "E29.3.21.0", {"start": v(5, -31.6) * mm, "end": v(5.94, -31.46) * mm});
            skLineSegment(sketch, "E29.6.21.0", {"start": v(4.08, -31.75) * mm, "end": v(3.4, -29.8) * mm});
            skLineSegment(sketch, "E29.9.21.0", {"start": v(5.94, -31.46) * mm, "end": v(5.97, -29.4) * mm});
            skLineSegment(sketch, "E29.1.22.0", {"start": v(9.89, -30.43) * mm, "end": v(9, -30.73) * mm});
            skLineSegment(sketch, "E29.3.22.0", {"start": v(9.89, -30.43) * mm, "end": v(10.78, -30.14) * mm});
            skLineSegment(sketch, "E29.6.22.0", {"start": v(9, -30.73) * mm, "end": v(8.03, -28.9) * mm});
            skLineSegment(sketch, "E29.9.22.0", {"start": v(10.78, -30.14) * mm, "end": v(10.5, -28.1) * mm});
            skLineSegment(sketch, "E29.1.23.0", {"start": v(14.53, -28.51) * mm, "end": v(13.69, -28.94) * mm});
            skLineSegment(sketch, "E29.3.23.0", {"start": v(14.53, -28.51) * mm, "end": v(15.37, -28.08) * mm});
            skLineSegment(sketch, "E29.6.23.0", {"start": v(13.69, -28.94) * mm, "end": v(12.45, -27.3) * mm});
            skLineSegment(sketch, "E29.9.23.0", {"start": v(15.37, -28.08) * mm, "end": v(14.77, -26.11) * mm});
            skLineSegment(sketch, "E29.1.24.0", {"start": v(18.8, -25.89) * mm, "end": v(18.05, -26.44) * mm});
            skLineSegment(sketch, "E29.3.24.0", {"start": v(18.8, -25.89) * mm, "end": v(19.57, -25.33) * mm});
            skLineSegment(sketch, "E29.6.24.0", {"start": v(18.05, -26.44) * mm, "end": v(16.57, -25.01) * mm});
            skLineSegment(sketch, "E29.9.24.0", {"start": v(19.57, -25.33) * mm, "end": v(18.67, -23.48) * mm});
            skLineSegment(sketch, "E29.1.25.0", {"start": v(22.63, -22.63) * mm, "end": v(21.96, -23.3) * mm});
            skLineSegment(sketch, "E29.3.25.0", {"start": v(22.63, -22.63) * mm, "end": v(23.3, -21.96) * mm});
            skLineSegment(sketch, "E29.6.25.0", {"start": v(21.96, -23.3) * mm, "end": v(20.27, -22.11) * mm});
            skLineSegment(sketch, "E29.9.25.0", {"start": v(23.3, -21.96) * mm, "end": v(22.11, -20.27) * mm});
            skLineSegment(sketch, "E29.1.26.0", {"start": v(25.89, -18.8) * mm, "end": v(25.33, -19.57) * mm});
            skLineSegment(sketch, "E29.3.26.0", {"start": v(25.89, -18.8) * mm, "end": v(26.44, -18.05) * mm});
            skLineSegment(sketch, "E29.6.26.0", {"start": v(25.33, -19.57) * mm, "end": v(23.48, -18.67) * mm});
            skLineSegment(sketch, "E29.9.26.0", {"start": v(26.44, -18.05) * mm, "end": v(25.01, -16.57) * mm});
            skLineSegment(sketch, "E29.1.27.0", {"start": v(28.51, -14.53) * mm, "end": v(28.08, -15.37) * mm});
            skLineSegment(sketch, "E29.3.27.0", {"start": v(28.51, -14.53) * mm, "end": v(28.94, -13.69) * mm});
            skLineSegment(sketch, "E29.6.27.0", {"start": v(28.08, -15.37) * mm, "end": v(26.11, -14.77) * mm});
            skLineSegment(sketch, "E29.9.27.0", {"start": v(28.94, -13.69) * mm, "end": v(27.3, -12.45) * mm});
            skLineSegment(sketch, "E29.1.28.0", {"start": v(30.43, -9.89) * mm, "end": v(30.14, -10.78) * mm});
            skLineSegment(sketch, "E29.3.28.0", {"start": v(30.43, -9.89) * mm, "end": v(30.73, -9) * mm});
            skLineSegment(sketch, "E29.6.28.0", {"start": v(30.14, -10.78) * mm, "end": v(28.1, -10.5) * mm});
            skLineSegment(sketch, "E29.9.28.0", {"start": v(30.73, -9) * mm, "end": v(28.9, -8.03) * mm});
            skLineSegment(sketch, "E29.1.29.0", {"start": v(31.6, -5) * mm, "end": v(31.46, -5.94) * mm});
            skLineSegment(sketch, "E29.3.29.0", {"start": v(31.6, -5) * mm, "end": v(31.75, -4.08) * mm});
            skLineSegment(sketch, "E29.6.29.0", {"start": v(31.46, -5.94) * mm, "end": v(29.4, -5.97) * mm});
            skLineSegment(sketch, "E29.9.29.0", {"start": v(31.75, -4.08) * mm, "end": v(29.8, -3.4) * mm});
            skLineSegment(sketch, "E29.1.30.0", {"start": v(32, 0) * mm, "end": v(32, -0.94) * mm});
            skLineSegment(sketch, "E29.3.30.0", {"start": v(32, 0) * mm, "end": v(32, 0.94) * mm});
            skLineSegment(sketch, "E29.6.30.0", {"start": v(32, -0.94) * mm, "end": v(29.97, -1.3) * mm});
            skLineSegment(sketch, "E29.9.30.0", {"start": v(32, 0.94) * mm, "end": v(29.97, 1.3) * mm});
            skLineSegment(sketch, "E29.1.31.0", {"start": v(31.6, 5) * mm, "end": v(31.75, 4.08) * mm});
            skLineSegment(sketch, "E29.3.31.0", {"start": v(31.6, 5) * mm, "end": v(31.46, 5.94) * mm});
            skLineSegment(sketch, "E29.6.31.0", {"start": v(31.75, 4.08) * mm, "end": v(29.8, 3.4) * mm});
            skLineSegment(sketch, "E29.9.31.0", {"start": v(31.46, 5.94) * mm, "end": v(29.4, 5.97) * mm});
            skLineSegment(sketch, "E29.1.32.0", {"start": v(30.43, 9.89) * mm, "end": v(30.73, 9) * mm});
            skLineSegment(sketch, "E29.3.32.0", {"start": v(30.43, 9.89) * mm, "end": v(30.14, 10.78) * mm});
            skLineSegment(sketch, "E29.6.32.0", {"start": v(30.73, 9) * mm, "end": v(28.9, 8.03) * mm});
            skLineSegment(sketch, "E29.9.32.0", {"start": v(30.14, 10.78) * mm, "end": v(28.1, 10.5) * mm});
            skLineSegment(sketch, "E29.1.33.0", {"start": v(28.51, 14.53) * mm, "end": v(28.94, 13.69) * mm});
            skLineSegment(sketch, "E29.3.33.0", {"start": v(28.51, 14.53) * mm, "end": v(28.08, 15.37) * mm});
            skLineSegment(sketch, "E29.6.33.0", {"start": v(28.94, 13.69) * mm, "end": v(27.3, 12.45) * mm});
            skLineSegment(sketch, "E29.9.33.0", {"start": v(28.08, 15.37) * mm, "end": v(26.11, 14.77) * mm});
            skLineSegment(sketch, "E29.1.34.0", {"start": v(25.89, 18.8) * mm, "end": v(26.44, 18.05) * mm});
            skLineSegment(sketch, "E29.3.34.0", {"start": v(25.89, 18.8) * mm, "end": v(25.33, 19.57) * mm});
            skLineSegment(sketch, "E29.6.34.0", {"start": v(26.44, 18.05) * mm, "end": v(25.01, 16.57) * mm});
            skLineSegment(sketch, "E29.9.34.0", {"start": v(25.33, 19.57) * mm, "end": v(23.48, 18.67) * mm});
            skLineSegment(sketch, "E29.1.35.0", {"start": v(22.63, 22.63) * mm, "end": v(23.3, 21.96) * mm});
            skLineSegment(sketch, "E29.3.35.0", {"start": v(22.63, 22.63) * mm, "end": v(21.96, 23.3) * mm});
            skLineSegment(sketch, "E29.6.35.0", {"start": v(23.3, 21.96) * mm, "end": v(22.11, 20.27) * mm});
            skLineSegment(sketch, "E29.9.35.0", {"start": v(21.96, 23.3) * mm, "end": v(20.27, 22.11) * mm});
            skLineSegment(sketch, "E29.1.36.0", {"start": v(18.8, 25.89) * mm, "end": v(19.57, 25.33) * mm});
            skLineSegment(sketch, "E29.3.36.0", {"start": v(18.8, 25.89) * mm, "end": v(18.05, 26.44) * mm});
            skLineSegment(sketch, "E29.6.36.0", {"start": v(19.57, 25.33) * mm, "end": v(18.67, 23.48) * mm});
            skLineSegment(sketch, "E29.9.36.0", {"start": v(18.05, 26.44) * mm, "end": v(16.57, 25.01) * mm});
            skLineSegment(sketch, "E29.1.37.0", {"start": v(14.53, 28.51) * mm, "end": v(15.37, 28.08) * mm});
            skLineSegment(sketch, "E29.3.37.0", {"start": v(14.53, 28.51) * mm, "end": v(13.69, 28.94) * mm});
            skLineSegment(sketch, "E29.6.37.0", {"start": v(15.37, 28.08) * mm, "end": v(14.77, 26.11) * mm});
            skLineSegment(sketch, "E29.9.37.0", {"start": v(13.69, 28.94) * mm, "end": v(12.45, 27.3) * mm});
            skLineSegment(sketch, "E29.1.38.0", {"start": v(9.89, 30.43) * mm, "end": v(10.78, 30.14) * mm});
            skLineSegment(sketch, "E29.3.38.0", {"start": v(9.89, 30.43) * mm, "end": v(9, 30.73) * mm});
            skLineSegment(sketch, "E29.6.38.0", {"start": v(10.78, 30.14) * mm, "end": v(10.5, 28.1) * mm});
            skLineSegment(sketch, "E29.9.38.0", {"start": v(9, 30.73) * mm, "end": v(8.03, 28.9) * mm});
            skLineSegment(sketch, "E29.1.39.0", {"start": v(5, 31.6) * mm, "end": v(5.94, 31.46) * mm});
            skLineSegment(sketch, "E29.3.39.0", {"start": v(5, 31.6) * mm, "end": v(4.08, 31.75) * mm});
            skLineSegment(sketch, "E29.6.39.0", {"start": v(5.94, 31.46) * mm, "end": v(5.97, 29.4) * mm});
            skLineSegment(sketch, "E29.9.39.0", {"start": v(4.08, 31.75) * mm, "end": v(3.4, 29.8) * mm});
            skSolve(sketch);
        }
        {
            var Q0;
            Q0 = qSketchRegion(id + "F14", true);
            extrude(context, id + "F15", {"entities" : qUnion([Q0]), "operationType" : NewBodyOperationType.ADD, "depth" : 4 * mm, "offsetDistance" : 25 * mm});
        }
        {
            var Q0;
            Q0=makeQuery(id+"F7.opExtrude","CAP_FACE",FACE,{"disambiguationData":[OSD([sQuery(id+"F0.wireOp",EDGE,"E0")])],"isStart":false});
            var sketch = newSketch(context, id + "F16", { "sketchPlane" : qUnion([Q0])});
            skCircle(sketch, "E30", {"center": v(40, 0) * mm, "radius": 7.5 * mm});
            skLineSegment(sketch, "E31", {"start": v(40, 0) * mm, "end": v(40, 7.5) * mm, "construction": true});
            skLineSegment(sketch, "E32", {"start": v(38.68, 7.38) * mm, "end": v(39.06, 9.5) * mm});
            skLineSegment(sketch, "E33", {"start": v(39.06, 9.5) * mm, "end": v(40.94, 9.5) * mm});
            skLineSegment(sketch, "E34.MirrorCS", {"start": v(41.32, 7.38) * mm, "end": v(40.94, 9.5) * mm});
            skLineSegment(sketch, "E35.1.0", {"start": v(33.65, 7.13) * mm, "end": v(35.18, 8.24) * mm});
            skLineSegment(sketch, "E35.1.1", {"start": v(36.72, 6.75) * mm, "end": v(35.18, 8.24) * mm});
            skLineSegment(sketch, "E35.1.2", {"start": v(34.6, 5.2) * mm, "end": v(33.65, 7.13) * mm});
            skLineSegment(sketch, "E35.2.0", {"start": v(30.67, 2.04) * mm, "end": v(31.26, 3.83) * mm});
            skLineSegment(sketch, "E35.2.1", {"start": v(33.38, 3.53) * mm, "end": v(31.26, 3.83) * mm});
            skLineSegment(sketch, "E35.2.2", {"start": v(32.57, 1.03) * mm, "end": v(30.67, 2.04) * mm});
            skLineSegment(sketch, "E36.1.3.0", {"start": v(31.26, -3.83) * mm, "end": v(30.67, -2.04) * mm});
            skLineSegment(sketch, "E36.3.3.0", {"start": v(32.57, -1.03) * mm, "end": v(30.67, -2.04) * mm});
            skLineSegment(sketch, "E36.6.3.0", {"start": v(33.38, -3.53) * mm, "end": v(31.26, -3.83) * mm});
            skLineSegment(sketch, "E36.1.4.0", {"start": v(35.18, -8.24) * mm, "end": v(33.65, -7.13) * mm});
            skLineSegment(sketch, "E36.3.4.0", {"start": v(34.6, -5.2) * mm, "end": v(33.65, -7.13) * mm});
            skLineSegment(sketch, "E36.6.4.0", {"start": v(36.72, -6.75) * mm, "end": v(35.18, -8.24) * mm});
            skLineSegment(sketch, "E36.1.5.0", {"start": v(40.94, -9.5) * mm, "end": v(39.06, -9.5) * mm});
            skLineSegment(sketch, "E36.3.5.0", {"start": v(38.68, -7.38) * mm, "end": v(39.06, -9.5) * mm});
            skLineSegment(sketch, "E36.6.5.0", {"start": v(41.32, -7.38) * mm, "end": v(40.94, -9.5) * mm});
            skLineSegment(sketch, "E36.1.6.0", {"start": v(46.35, -7.13) * mm, "end": v(44.82, -8.24) * mm});
            skLineSegment(sketch, "E36.3.6.0", {"start": v(43.28, -6.75) * mm, "end": v(44.82, -8.24) * mm});
            skLineSegment(sketch, "E36.6.6.0", {"start": v(45.4, -5.2) * mm, "end": v(46.35, -7.13) * mm});
            skLineSegment(sketch, "E36.1.7.0", {"start": v(49.33, -2.04) * mm, "end": v(48.74, -3.83) * mm});
            skLineSegment(sketch, "E36.3.7.0", {"start": v(46.62, -3.53) * mm, "end": v(48.74, -3.83) * mm});
            skLineSegment(sketch, "E36.6.7.0", {"start": v(47.43, -1.03) * mm, "end": v(49.33, -2.04) * mm});
            skLineSegment(sketch, "E36.1.8.0", {"start": v(48.74, 3.83) * mm, "end": v(49.33, 2.04) * mm});
            skLineSegment(sketch, "E36.3.8.0", {"start": v(47.43, 1.03) * mm, "end": v(49.33, 2.04) * mm});
            skLineSegment(sketch, "E36.6.8.0", {"start": v(46.62, 3.53) * mm, "end": v(48.74, 3.83) * mm});
            skLineSegment(sketch, "E36.1.9.0", {"start": v(44.82, 8.24) * mm, "end": v(46.35, 7.13) * mm});
            skLineSegment(sketch, "E36.3.9.0", {"start": v(45.4, 5.2) * mm, "end": v(46.35, 7.13) * mm});
            skLineSegment(sketch, "E36.6.9.0", {"start": v(43.28, 6.75) * mm, "end": v(44.82, 8.24) * mm});
            skSolve(sketch);
        }
        {
            var Q0;
            Q0 = qSketchRegion(id + "F16", true);
            extrude(context, id + "F17", {"entities" : qUnion([Q0]), "operationType" : NewBodyOperationType.ADD, "depth" : 4 * mm, "offsetDistance" : 25 * mm});
        }
        {
            var Q0;
            Q0=makeQuery(id+"F17.opExtrude","CAP_FACE",FACE,{"disambiguationData":[OSD([sQuery(id+"F16.wireOp",EDGE,"E30"),sQuery(id+"F16.wireOp",EDGE,"E32"),sQuery(id+"F16.wireOp",EDGE,"E33"),sQuery(id+"F16.wireOp",EDGE,"E34.MirrorCS"),sQuery(id+"F16.wireOp",EDGE,"E35.1.0"),sQuery(id+"F16.wireOp",EDGE,"E35.1.1"),sQuery(id+"F16.wireOp",EDGE,"E35.1.2"),sQuery(id+"F16.wireOp",EDGE,"E35.2.0"),sQuery(id+"F16.wireOp",EDGE,"E35.2.1"),sQuery(id+"F16.wireOp",EDGE,"E35.2.2"),sQuery(id+"F16.wireOp",EDGE,"E36.1.3.0"),sQuery(id+"F16.wireOp",EDGE,"E36.3.3.0"),sQuery(id+"F16.wireOp",EDGE,"E36.6.3.0"),sQuery(id+"F16.wireOp",EDGE,"E36.1.4.0"),sQuery(id+"F16.wireOp",EDGE,"E36.3.4.0"),sQuery(id+"F16.wireOp",EDGE,"E36.6.4.0"),sQuery(id+"F16.wireOp",EDGE,"E36.1.5.0"),sQuery(id+"F16.wireOp",EDGE,"E36.3.5.0"),sQuery(id+"F16.wireOp",EDGE,"E36.6.5.0"),sQuery(id+"F16.wireOp",EDGE,"E36.1.6.0"),sQuery(id+"F16.wireOp",EDGE,"E36.3.6.0"),sQuery(id+"F16.wireOp",EDGE,"E36.6.6.0"),sQuery(id+"F16.wireOp",EDGE,"E36.1.7.0"),sQuery(id+"F16.wireOp",EDGE,"E36.3.7.0"),sQuery(id+"F16.wireOp",EDGE,"E36.6.7.0"),sQuery(id+"F16.wireOp",EDGE,"E36.1.8.0"),sQuery(id+"F16.wireOp",EDGE,"E36.3.8.0"),sQuery(id+"F16.wireOp",EDGE,"E36.6.8.0"),sQuery(id+"F16.wireOp",EDGE,"E36.1.9.0"),sQuery(id+"F16.wireOp",EDGE,"E36.3.9.0"),sQuery(id+"F16.wireOp",EDGE,"E36.6.9.0")])],"isStart":false});
            var sketch = newSketch(context, id + "F18", { "sketchPlane" : qUnion([Q0])});
            skCircle(sketch, "E37.0", {"center": v(40, 0) * mm, "radius": 3 * mm});
            skSolve(sketch);
        }
        {
            var Q0;
            Q0 = qSketchRegion(id + "F18", true);
            extrude(context, id + "F19", {"entities" : qUnion([Q0]), "operationType" : NewBodyOperationType.ADD, "depth" : 2 * mm, "offsetDistance" : 25 * mm});
        }
        {
            var Q0;
            Q0=makeQuery(id+"F19.opExtrude","CAP_FACE",FACE,{"disambiguationData":[OSD([sQuery(id+"F18.wireOp",EDGE,"E37.0")])],"isStart":false});
            var sketch = newSketch(context, id + "F20", { "sketchPlane" : qUnion([Q0])});
            skCircle(sketch, "E38", {"center": v(0, 0) * mm, "radius": 98 * mm});
            skCircle(sketch, "E39.0", {"center": v(0, 0) * mm, "radius": 5 * mm});
            skSolve(sketch);
        }
        {
            var Q0;
            Q0 = qSketchRegion(id + "F20", true);
            extrude(context, id + "F21", {"entities" : qUnion([Q0]), "depth" : 1 * mm, "offsetDistance" : 25 * mm});
        }
        {
            var Q0;
            Q0=makeQuery(id+"F21.opExtrude","SWEPT_BODY",BODY,{"disambiguationData":[OSD([sQuery(id+"F20.wireOp",EDGE,"E38"),sQuery(id+"F20.wireOp",EDGE,"E39.0")])]});
            var Q1;
            Q1=makeQuery(id+"F1.opExtrude","SWEPT_BODY",BODY,{"disambiguationData":[OSD([sQuery(id+"F0.wireOp",EDGE,"E0")])]});
            booleanBodies(context, id + "F22", {"operationType" : BooleanOperationType.SUBTRACTION, "tools" : qUnion([Q0]), "targets" : qUnion([Q1]), "keepTools" : true});
        }
        {
            var Q0;
            Q0=makeQuery(id+"F21.opExtrude","CAP_FACE",FACE,{"disambiguationData":[OSD([sQuery(id+"F20.wireOp",EDGE,"E38"),sQuery(id+"F20.wireOp",EDGE,"E39.0")])],"isStart":true});
            var sketch = newSketch(context, id + "F23", { "sketchPlane" : qUnion([Q0])});
            skCircle(sketch, "E40.0", {"center": v(-40, 0) * mm, "radius": 3 * mm});
            skCircle(sketch, "E41", {"center": v(-40, 0) * mm, "radius": 5 * mm});
            skSolve(sketch);
        }
        {
            var Q0;
            Q0 = qSketchRegion(id + "F23", true);
            extrude(context, id + "F24", {"entities" : qUnion([Q0]), "operationType" : NewBodyOperationType.ADD, "endBound" : BoundingType.UP_TO_NEXT, "depth" : 25 * mm, "offsetDistance" : 25 * mm});
        }
        {
            var Q0;
            Q0=makeQuery(id+"F21.opExtrude","CAP_FACE",FACE,{"disambiguationData":[OSD([sQuery(id+"F20.wireOp",EDGE,"E38"),sQuery(id+"F20.wireOp",EDGE,"E39.0")])],"isStart":false});
            var sketch = newSketch(context, id + "F25", { "sketchPlane" : qUnion([Q0])});
            skLineSegment(sketch, "E42.bottom", {"start": v(1.5, 71) * mm, "end": v(-1.5, 71) * mm});
            skLineSegment(sketch, "E42.top", {"start": v(1.5, 91) * mm, "end": v(-1.5, 91) * mm});
            skLineSegment(sketch, "E42.left", {"start": v(1.5, 71) * mm, "end": v(1.5, 91) * mm});
            skLineSegment(sketch, "E42.right", {"start": v(-1.5, 71) * mm, "end": v(-1.5, 91) * mm});
            skPoint(sketch, "E42.middle", {"position": v(0, 81) * mm});
            skLineSegment(sketch, "E43.1.0", {"start": v(-44.2, 79.56) * mm, "end": v(-46.8, 78.06) * mm});
            skLineSegment(sketch, "E43.1.1", {"start": v(-34.2, 62.24) * mm, "end": v(-44.2, 79.56) * mm});
            skLineSegment(sketch, "E43.1.2", {"start": v(-36.8, 60.74) * mm, "end": v(-46.8, 78.06) * mm});
            skLineSegment(sketch, "E43.1.3", {"start": v(-34.2, 62.24) * mm, "end": v(-36.8, 60.74) * mm});
            skLineSegment(sketch, "E43.2.0", {"start": v(-78.06, 46.8) * mm, "end": v(-79.56, 44.2) * mm});
            skLineSegment(sketch, "E43.2.1", {"start": v(-60.74, 36.8) * mm, "end": v(-78.06, 46.8) * mm});
            skLineSegment(sketch, "E43.2.2", {"start": v(-62.24, 34.2) * mm, "end": v(-79.56, 44.2) * mm});
            skLineSegment(sketch, "E43.2.3", {"start": v(-60.74, 36.8) * mm, "end": v(-62.24, 34.2) * mm});
            skPoint(sketch, "E43.center", {"position": v(0, 0) * mm});
            skLineSegment(sketch, "E44.2.3.0", {"start": v(-91, 1.5) * mm, "end": v(-91, -1.5) * mm});
            skLineSegment(sketch, "E44.3.3.0", {"start": v(-71, 1.5) * mm, "end": v(-91, 1.5) * mm});
            skLineSegment(sketch, "E44.6.3.0", {"start": v(-71, -1.5) * mm, "end": v(-91, -1.5) * mm});
            skLineSegment(sketch, "E44.9.3.0", {"start": v(-71, 1.5) * mm, "end": v(-71, -1.5) * mm});
            skLineSegment(sketch, "E44.2.4.0", {"start": v(-79.56, -44.2) * mm, "end": v(-78.06, -46.8) * mm});
            skLineSegment(sketch, "E44.3.4.0", {"start": v(-62.24, -34.2) * mm, "end": v(-79.56, -44.2) * mm});
            skLineSegment(sketch, "E44.6.4.0", {"start": v(-60.74, -36.8) * mm, "end": v(-78.06, -46.8) * mm});
            skLineSegment(sketch, "E44.9.4.0", {"start": v(-62.24, -34.2) * mm, "end": v(-60.74, -36.8) * mm});
            skLineSegment(sketch, "E44.2.5.0", {"start": v(-46.8, -78.06) * mm, "end": v(-44.2, -79.56) * mm});
            skLineSegment(sketch, "E44.3.5.0", {"start": v(-36.8, -60.74) * mm, "end": v(-46.8, -78.06) * mm});
            skLineSegment(sketch, "E44.6.5.0", {"start": v(-34.2, -62.24) * mm, "end": v(-44.2, -79.56) * mm});
            skLineSegment(sketch, "E44.9.5.0", {"start": v(-36.8, -60.74) * mm, "end": v(-34.2, -62.24) * mm});
            skLineSegment(sketch, "E44.2.6.0", {"start": v(-1.5, -91) * mm, "end": v(1.5, -91) * mm});
            skLineSegment(sketch, "E44.3.6.0", {"start": v(-1.5, -71) * mm, "end": v(-1.5, -91) * mm});
            skLineSegment(sketch, "E44.6.6.0", {"start": v(1.5, -71) * mm, "end": v(1.5, -91) * mm});
            skLineSegment(sketch, "E44.9.6.0", {"start": v(-1.5, -71) * mm, "end": v(1.5, -71) * mm});
            skLineSegment(sketch, "E44.2.7.0", {"start": v(44.2, -79.56) * mm, "end": v(46.8, -78.06) * mm});
            skLineSegment(sketch, "E44.3.7.0", {"start": v(34.2, -62.24) * mm, "end": v(44.2, -79.56) * mm});
            skLineSegment(sketch, "E44.6.7.0", {"start": v(36.8, -60.74) * mm, "end": v(46.8, -78.06) * mm});
            skLineSegment(sketch, "E44.9.7.0", {"start": v(34.2, -62.24) * mm, "end": v(36.8, -60.74) * mm});
            skLineSegment(sketch, "E44.2.8.0", {"start": v(78.06, -46.8) * mm, "end": v(79.56, -44.2) * mm});
            skLineSegment(sketch, "E44.3.8.0", {"start": v(60.74, -36.8) * mm, "end": v(78.06, -46.8) * mm});
            skLineSegment(sketch, "E44.6.8.0", {"start": v(62.24, -34.2) * mm, "end": v(79.56, -44.2) * mm});
            skLineSegment(sketch, "E44.9.8.0", {"start": v(60.74, -36.8) * mm, "end": v(62.24, -34.2) * mm});
            skLineSegment(sketch, "E44.2.9.0", {"start": v(91, -1.5) * mm, "end": v(91, 1.5) * mm});
            skLineSegment(sketch, "E44.3.9.0", {"start": v(71, -1.5) * mm, "end": v(91, -1.5) * mm});
            skLineSegment(sketch, "E44.6.9.0", {"start": v(71, 1.5) * mm, "end": v(91, 1.5) * mm});
            skLineSegment(sketch, "E44.9.9.0", {"start": v(71, -1.5) * mm, "end": v(71, 1.5) * mm});
            skLineSegment(sketch, "E44.2.10.0", {"start": v(79.56, 44.2) * mm, "end": v(78.06, 46.8) * mm});
            skLineSegment(sketch, "E44.3.10.0", {"start": v(62.24, 34.2) * mm, "end": v(79.56, 44.2) * mm});
            skLineSegment(sketch, "E44.6.10.0", {"start": v(60.74, 36.8) * mm, "end": v(78.06, 46.8) * mm});
            skLineSegment(sketch, "E44.9.10.0", {"start": v(62.24, 34.2) * mm, "end": v(60.74, 36.8) * mm});
            skLineSegment(sketch, "E44.2.11.0", {"start": v(46.8, 78.06) * mm, "end": v(44.2, 79.56) * mm});
            skLineSegment(sketch, "E44.3.11.0", {"start": v(36.8, 60.74) * mm, "end": v(46.8, 78.06) * mm});
            skLineSegment(sketch, "E44.6.11.0", {"start": v(34.2, 62.24) * mm, "end": v(44.2, 79.56) * mm});
            skLineSegment(sketch, "E44.9.11.0", {"start": v(36.8, 60.74) * mm, "end": v(34.2, 62.24) * mm});
            skSolve(sketch);
        }
        {
            var Q0;
            Q0 = qSketchRegion(id + "F25", true);
            extrude(context, id + "F26", {"entities" : qUnion([Q0]), "operationType" : NewBodyOperationType.REMOVE, "oppositeDirection" : true, "depth" : 0.5 * mm, "offsetDistance" : 25 * mm});
        }
        {
            var Q0;
            Q0=makeQuery(id+"F21.opExtrude","CAP_FACE",FACE,{"disambiguationData":[OSD([sQuery(id+"F20.wireOp",EDGE,"E38"),sQuery(id+"F20.wireOp",EDGE,"E39.0")])],"isStart":false});
            var sketch = newSketch(context, id + "F27", { "sketchPlane" : qUnion([Q0])});
            skLineSegment(sketch, "E45.bottom", {"start": v(0.75, 78.5) * mm, "end": v(-0.75, 78.5) * mm});
            skLineSegment(sketch, "E45.top", {"start": v(0.75, 90.5) * mm, "end": v(-0.75, 90.5) * mm});
            skLineSegment(sketch, "E45.left", {"start": v(0.75, 78.5) * mm, "end": v(0.75, 90.5) * mm});
            skLineSegment(sketch, "E45.right", {"start": v(-0.75, 78.5) * mm, "end": v(-0.75, 90.5) * mm});
            skPoint(sketch, "E45.middle", {"position": v(0, 84.5) * mm});
            skLineSegment(sketch, "E46.1.0", {"start": v(-8.71, 90.08) * mm, "end": v(-10.2, 89.93) * mm});
            skLineSegment(sketch, "E46.1.1", {"start": v(-7.46, 78.15) * mm, "end": v(-8.71, 90.08) * mm});
            skLineSegment(sketch, "E46.1.2", {"start": v(-8.95, 78) * mm, "end": v(-10.2, 89.93) * mm});
            skLineSegment(sketch, "E46.1.3", {"start": v(-7.46, 78.15) * mm, "end": v(-8.95, 78) * mm});
            skLineSegment(sketch, "E46.2.0", {"start": v(-18.08, 88.68) * mm, "end": v(-19.55, 88.37) * mm});
            skLineSegment(sketch, "E46.2.1", {"start": v(-15.59, 76.94) * mm, "end": v(-18.08, 88.68) * mm});
            skLineSegment(sketch, "E46.2.2", {"start": v(-17.05, 76.63) * mm, "end": v(-19.55, 88.37) * mm});
            skLineSegment(sketch, "E46.2.3", {"start": v(-15.59, 76.94) * mm, "end": v(-17.05, 76.63) * mm});
            skPoint(sketch, "E46.center", {"position": v(0, 0) * mm});
            skLineSegment(sketch, "E47.2.3.0", {"start": v(-27.25, 86.3) * mm, "end": v(-28.68, 85.84) * mm});
            skLineSegment(sketch, "E47.3.3.0", {"start": v(-23.54, 74.89) * mm, "end": v(-27.25, 86.3) * mm});
            skLineSegment(sketch, "E47.6.3.0", {"start": v(-24.97, 74.43) * mm, "end": v(-28.68, 85.84) * mm});
            skLineSegment(sketch, "E47.9.3.0", {"start": v(-23.54, 74.89) * mm, "end": v(-24.97, 74.43) * mm});
            skLineSegment(sketch, "E47.2.4.0", {"start": v(-36.12, 82.98) * mm, "end": v(-37.5, 82.37) * mm});
            skLineSegment(sketch, "E47.3.4.0", {"start": v(-31.24, 72.02) * mm, "end": v(-36.12, 82.98) * mm});
            skLineSegment(sketch, "E47.6.4.0", {"start": v(-32.61, 71.4) * mm, "end": v(-37.5, 82.37) * mm});
            skLineSegment(sketch, "E47.9.4.0", {"start": v(-31.24, 72.02) * mm, "end": v(-32.61, 71.4) * mm});
            skLineSegment(sketch, "E47.2.5.0", {"start": v(-44.6, 78.75) * mm, "end": v(-45.9, 78) * mm});
            skLineSegment(sketch, "E47.3.5.0", {"start": v(-38.6, 68.36) * mm, "end": v(-44.6, 78.75) * mm});
            skLineSegment(sketch, "E47.6.5.0", {"start": v(-39.9, 67.6) * mm, "end": v(-45.9, 78) * mm});
            skLineSegment(sketch, "E47.9.5.0", {"start": v(-38.6, 68.36) * mm, "end": v(-39.9, 67.6) * mm});
            skLineSegment(sketch, "E47.2.6.0", {"start": v(-52.59, 73.66) * mm, "end": v(-53.8, 72.78) * mm});
            skLineSegment(sketch, "E47.3.6.0", {"start": v(-45.53, 63.95) * mm, "end": v(-52.59, 73.66) * mm});
            skLineSegment(sketch, "E47.6.6.0", {"start": v(-46.75, 63.07) * mm, "end": v(-53.8, 72.78) * mm});
            skLineSegment(sketch, "E47.9.6.0", {"start": v(-45.53, 63.95) * mm, "end": v(-46.75, 63.07) * mm});
            skLineSegment(sketch, "E47.2.7.0", {"start": v(-60, 67.76) * mm, "end": v(-61.11, 66.75) * mm});
            skLineSegment(sketch, "E47.3.7.0", {"start": v(-51.97, 58.84) * mm, "end": v(-60, 67.76) * mm});
            skLineSegment(sketch, "E47.6.7.0", {"start": v(-53.08, 57.84) * mm, "end": v(-61.11, 66.75) * mm});
            skLineSegment(sketch, "E47.9.7.0", {"start": v(-51.97, 58.84) * mm, "end": v(-53.08, 57.84) * mm});
            skLineSegment(sketch, "E47.2.8.0", {"start": v(-66.75, 61.11) * mm, "end": v(-67.76, 60) * mm});
            skLineSegment(sketch, "E47.3.8.0", {"start": v(-57.84, 53.08) * mm, "end": v(-66.75, 61.11) * mm});
            skLineSegment(sketch, "E47.6.8.0", {"start": v(-58.84, 51.97) * mm, "end": v(-67.76, 60) * mm});
            skLineSegment(sketch, "E47.9.8.0", {"start": v(-57.84, 53.08) * mm, "end": v(-58.84, 51.97) * mm});
            skLineSegment(sketch, "E47.2.9.0", {"start": v(-72.78, 53.8) * mm, "end": v(-73.66, 52.59) * mm});
            skLineSegment(sketch, "E47.3.9.0", {"start": v(-63.07, 46.75) * mm, "end": v(-72.78, 53.8) * mm});
            skLineSegment(sketch, "E47.6.9.0", {"start": v(-63.95, 45.53) * mm, "end": v(-73.66, 52.59) * mm});
            skLineSegment(sketch, "E47.9.9.0", {"start": v(-63.07, 46.75) * mm, "end": v(-63.95, 45.53) * mm});
            skLineSegment(sketch, "E47.2.10.0", {"start": v(-78, 45.9) * mm, "end": v(-78.75, 44.6) * mm});
            skLineSegment(sketch, "E47.3.10.0", {"start": v(-67.6, 39.9) * mm, "end": v(-78, 45.9) * mm});
            skLineSegment(sketch, "E47.6.10.0", {"start": v(-68.36, 38.6) * mm, "end": v(-78.75, 44.6) * mm});
            skLineSegment(sketch, "E47.9.10.0", {"start": v(-67.6, 39.9) * mm, "end": v(-68.36, 38.6) * mm});
            skLineSegment(sketch, "E47.2.11.0", {"start": v(-82.37, 37.5) * mm, "end": v(-82.98, 36.12) * mm});
            skLineSegment(sketch, "E47.3.11.0", {"start": v(-71.4, 32.61) * mm, "end": v(-82.37, 37.5) * mm});
            skLineSegment(sketch, "E47.6.11.0", {"start": v(-72.02, 31.24) * mm, "end": v(-82.98, 36.12) * mm});
            skLineSegment(sketch, "E47.9.11.0", {"start": v(-71.4, 32.61) * mm, "end": v(-72.02, 31.24) * mm});
            skLineSegment(sketch, "E47.2.12.0", {"start": v(-85.84, 28.68) * mm, "end": v(-86.3, 27.25) * mm});
            skLineSegment(sketch, "E47.3.12.0", {"start": v(-74.43, 24.97) * mm, "end": v(-85.84, 28.68) * mm});
            skLineSegment(sketch, "E47.6.12.0", {"start": v(-74.89, 23.54) * mm, "end": v(-86.3, 27.25) * mm});
            skLineSegment(sketch, "E47.9.12.0", {"start": v(-74.43, 24.97) * mm, "end": v(-74.89, 23.54) * mm});
            skLineSegment(sketch, "E47.2.13.0", {"start": v(-88.37, 19.55) * mm, "end": v(-88.68, 18.08) * mm});
            skLineSegment(sketch, "E47.3.13.0", {"start": v(-76.63, 17.05) * mm, "end": v(-88.37, 19.55) * mm});
            skLineSegment(sketch, "E47.6.13.0", {"start": v(-76.94, 15.59) * mm, "end": v(-88.68, 18.08) * mm});
            skLineSegment(sketch, "E47.9.13.0", {"start": v(-76.63, 17.05) * mm, "end": v(-76.94, 15.59) * mm});
            skLineSegment(sketch, "E47.2.14.0", {"start": v(-89.93, 10.2) * mm, "end": v(-90.08, 8.71) * mm});
            skLineSegment(sketch, "E47.3.14.0", {"start": v(-78, 8.95) * mm, "end": v(-89.93, 10.2) * mm});
            skLineSegment(sketch, "E47.6.14.0", {"start": v(-78.15, 7.46) * mm, "end": v(-90.08, 8.71) * mm});
            skLineSegment(sketch, "E47.9.14.0", {"start": v(-78, 8.95) * mm, "end": v(-78.15, 7.46) * mm});
            skLineSegment(sketch, "E47.2.15.0", {"start": v(-90.5, 0.75) * mm, "end": v(-90.5, -0.75) * mm});
            skLineSegment(sketch, "E47.3.15.0", {"start": v(-78.5, 0.75) * mm, "end": v(-90.5, 0.75) * mm});
            skLineSegment(sketch, "E47.6.15.0", {"start": v(-78.5, -0.75) * mm, "end": v(-90.5, -0.75) * mm});
            skLineSegment(sketch, "E47.9.15.0", {"start": v(-78.5, 0.75) * mm, "end": v(-78.5, -0.75) * mm});
            skLineSegment(sketch, "E47.2.16.0", {"start": v(-90.08, -8.71) * mm, "end": v(-89.93, -10.2) * mm});
            skLineSegment(sketch, "E47.3.16.0", {"start": v(-78.15, -7.46) * mm, "end": v(-90.08, -8.71) * mm});
            skLineSegment(sketch, "E47.6.16.0", {"start": v(-78, -8.95) * mm, "end": v(-89.93, -10.2) * mm});
            skLineSegment(sketch, "E47.9.16.0", {"start": v(-78.15, -7.46) * mm, "end": v(-78, -8.95) * mm});
            skLineSegment(sketch, "E47.2.17.0", {"start": v(-88.68, -18.08) * mm, "end": v(-88.37, -19.55) * mm});
            skLineSegment(sketch, "E47.3.17.0", {"start": v(-76.94, -15.59) * mm, "end": v(-88.68, -18.08) * mm});
            skLineSegment(sketch, "E47.6.17.0", {"start": v(-76.63, -17.05) * mm, "end": v(-88.37, -19.55) * mm});
            skLineSegment(sketch, "E47.9.17.0", {"start": v(-76.94, -15.59) * mm, "end": v(-76.63, -17.05) * mm});
            skLineSegment(sketch, "E47.2.18.0", {"start": v(-86.3, -27.25) * mm, "end": v(-85.84, -28.68) * mm});
            skLineSegment(sketch, "E47.3.18.0", {"start": v(-74.89, -23.54) * mm, "end": v(-86.3, -27.25) * mm});
            skLineSegment(sketch, "E47.6.18.0", {"start": v(-74.43, -24.97) * mm, "end": v(-85.84, -28.68) * mm});
            skLineSegment(sketch, "E47.9.18.0", {"start": v(-74.89, -23.54) * mm, "end": v(-74.43, -24.97) * mm});
            skLineSegment(sketch, "E47.2.19.0", {"start": v(-82.98, -36.12) * mm, "end": v(-82.37, -37.5) * mm});
            skLineSegment(sketch, "E47.3.19.0", {"start": v(-72.02, -31.24) * mm, "end": v(-82.98, -36.12) * mm});
            skLineSegment(sketch, "E47.6.19.0", {"start": v(-71.4, -32.61) * mm, "end": v(-82.37, -37.5) * mm});
            skLineSegment(sketch, "E47.9.19.0", {"start": v(-72.02, -31.24) * mm, "end": v(-71.4, -32.61) * mm});
            skLineSegment(sketch, "E47.2.20.0", {"start": v(-78.75, -44.6) * mm, "end": v(-78, -45.9) * mm});
            skLineSegment(sketch, "E47.3.20.0", {"start": v(-68.36, -38.6) * mm, "end": v(-78.75, -44.6) * mm});
            skLineSegment(sketch, "E47.6.20.0", {"start": v(-67.6, -39.9) * mm, "end": v(-78, -45.9) * mm});
            skLineSegment(sketch, "E47.9.20.0", {"start": v(-68.36, -38.6) * mm, "end": v(-67.6, -39.9) * mm});
            skLineSegment(sketch, "E47.2.21.0", {"start": v(-73.66, -52.59) * mm, "end": v(-72.78, -53.8) * mm});
            skLineSegment(sketch, "E47.3.21.0", {"start": v(-63.95, -45.53) * mm, "end": v(-73.66, -52.59) * mm});
            skLineSegment(sketch, "E47.6.21.0", {"start": v(-63.07, -46.75) * mm, "end": v(-72.78, -53.8) * mm});
            skLineSegment(sketch, "E47.9.21.0", {"start": v(-63.95, -45.53) * mm, "end": v(-63.07, -46.75) * mm});
            skLineSegment(sketch, "E47.2.22.0", {"start": v(-67.76, -60) * mm, "end": v(-66.75, -61.11) * mm});
            skLineSegment(sketch, "E47.3.22.0", {"start": v(-58.84, -51.97) * mm, "end": v(-67.76, -60) * mm});
            skLineSegment(sketch, "E47.6.22.0", {"start": v(-57.84, -53.08) * mm, "end": v(-66.75, -61.11) * mm});
            skLineSegment(sketch, "E47.9.22.0", {"start": v(-58.84, -51.97) * mm, "end": v(-57.84, -53.08) * mm});
            skLineSegment(sketch, "E47.2.23.0", {"start": v(-61.11, -66.75) * mm, "end": v(-60, -67.76) * mm});
            skLineSegment(sketch, "E47.3.23.0", {"start": v(-53.08, -57.84) * mm, "end": v(-61.11, -66.75) * mm});
            skLineSegment(sketch, "E47.6.23.0", {"start": v(-51.97, -58.84) * mm, "end": v(-60, -67.76) * mm});
            skLineSegment(sketch, "E47.9.23.0", {"start": v(-53.08, -57.84) * mm, "end": v(-51.97, -58.84) * mm});
            skLineSegment(sketch, "E47.2.24.0", {"start": v(-53.8, -72.78) * mm, "end": v(-52.59, -73.66) * mm});
            skLineSegment(sketch, "E47.3.24.0", {"start": v(-46.75, -63.07) * mm, "end": v(-53.8, -72.78) * mm});
            skLineSegment(sketch, "E47.6.24.0", {"start": v(-45.53, -63.95) * mm, "end": v(-52.59, -73.66) * mm});
            skLineSegment(sketch, "E47.9.24.0", {"start": v(-46.75, -63.07) * mm, "end": v(-45.53, -63.95) * mm});
            skLineSegment(sketch, "E47.2.25.0", {"start": v(-45.9, -78) * mm, "end": v(-44.6, -78.75) * mm});
            skLineSegment(sketch, "E47.3.25.0", {"start": v(-39.9, -67.6) * mm, "end": v(-45.9, -78) * mm});
            skLineSegment(sketch, "E47.6.25.0", {"start": v(-38.6, -68.36) * mm, "end": v(-44.6, -78.75) * mm});
            skLineSegment(sketch, "E47.9.25.0", {"start": v(-39.9, -67.6) * mm, "end": v(-38.6, -68.36) * mm});
            skLineSegment(sketch, "E47.2.26.0", {"start": v(-37.5, -82.37) * mm, "end": v(-36.12, -82.98) * mm});
            skLineSegment(sketch, "E47.3.26.0", {"start": v(-32.61, -71.4) * mm, "end": v(-37.5, -82.37) * mm});
            skLineSegment(sketch, "E47.6.26.0", {"start": v(-31.24, -72.02) * mm, "end": v(-36.12, -82.98) * mm});
            skLineSegment(sketch, "E47.9.26.0", {"start": v(-32.61, -71.4) * mm, "end": v(-31.24, -72.02) * mm});
            skLineSegment(sketch, "E47.2.27.0", {"start": v(-28.68, -85.84) * mm, "end": v(-27.25, -86.3) * mm});
            skLineSegment(sketch, "E47.3.27.0", {"start": v(-24.97, -74.43) * mm, "end": v(-28.68, -85.84) * mm});
            skLineSegment(sketch, "E47.6.27.0", {"start": v(-23.54, -74.89) * mm, "end": v(-27.25, -86.3) * mm});
            skLineSegment(sketch, "E47.9.27.0", {"start": v(-24.97, -74.43) * mm, "end": v(-23.54, -74.89) * mm});
            skLineSegment(sketch, "E47.2.28.0", {"start": v(-19.55, -88.37) * mm, "end": v(-18.08, -88.68) * mm});
            skLineSegment(sketch, "E47.3.28.0", {"start": v(-17.05, -76.63) * mm, "end": v(-19.55, -88.37) * mm});
            skLineSegment(sketch, "E47.6.28.0", {"start": v(-15.59, -76.94) * mm, "end": v(-18.08, -88.68) * mm});
            skLineSegment(sketch, "E47.9.28.0", {"start": v(-17.05, -76.63) * mm, "end": v(-15.59, -76.94) * mm});
            skLineSegment(sketch, "E47.2.29.0", {"start": v(-10.2, -89.93) * mm, "end": v(-8.71, -90.08) * mm});
            skLineSegment(sketch, "E47.3.29.0", {"start": v(-8.95, -78) * mm, "end": v(-10.2, -89.93) * mm});
            skLineSegment(sketch, "E47.6.29.0", {"start": v(-7.46, -78.15) * mm, "end": v(-8.71, -90.08) * mm});
            skLineSegment(sketch, "E47.9.29.0", {"start": v(-8.95, -78) * mm, "end": v(-7.46, -78.15) * mm});
            skLineSegment(sketch, "E47.2.30.0", {"start": v(-0.75, -90.5) * mm, "end": v(0.75, -90.5) * mm});
            skLineSegment(sketch, "E47.3.30.0", {"start": v(-0.75, -78.5) * mm, "end": v(-0.75, -90.5) * mm});
            skLineSegment(sketch, "E47.6.30.0", {"start": v(0.75, -78.5) * mm, "end": v(0.75, -90.5) * mm});
            skLineSegment(sketch, "E47.9.30.0", {"start": v(-0.75, -78.5) * mm, "end": v(0.75, -78.5) * mm});
            skLineSegment(sketch, "E47.2.31.0", {"start": v(8.71, -90.08) * mm, "end": v(10.2, -89.93) * mm});
            skLineSegment(sketch, "E47.3.31.0", {"start": v(7.46, -78.15) * mm, "end": v(8.71, -90.08) * mm});
            skLineSegment(sketch, "E47.6.31.0", {"start": v(8.95, -78) * mm, "end": v(10.2, -89.93) * mm});
            skLineSegment(sketch, "E47.9.31.0", {"start": v(7.46, -78.15) * mm, "end": v(8.95, -78) * mm});
            skLineSegment(sketch, "E47.2.32.0", {"start": v(18.08, -88.68) * mm, "end": v(19.55, -88.37) * mm});
            skLineSegment(sketch, "E47.3.32.0", {"start": v(15.59, -76.94) * mm, "end": v(18.08, -88.68) * mm});
            skLineSegment(sketch, "E47.6.32.0", {"start": v(17.05, -76.63) * mm, "end": v(19.55, -88.37) * mm});
            skLineSegment(sketch, "E47.9.32.0", {"start": v(15.59, -76.94) * mm, "end": v(17.05, -76.63) * mm});
            skLineSegment(sketch, "E47.2.33.0", {"start": v(27.25, -86.3) * mm, "end": v(28.68, -85.84) * mm});
            skLineSegment(sketch, "E47.3.33.0", {"start": v(23.54, -74.89) * mm, "end": v(27.25, -86.3) * mm});
            skLineSegment(sketch, "E47.6.33.0", {"start": v(24.97, -74.43) * mm, "end": v(28.68, -85.84) * mm});
            skLineSegment(sketch, "E47.9.33.0", {"start": v(23.54, -74.89) * mm, "end": v(24.97, -74.43) * mm});
            skLineSegment(sketch, "E47.2.34.0", {"start": v(36.12, -82.98) * mm, "end": v(37.5, -82.37) * mm});
            skLineSegment(sketch, "E47.3.34.0", {"start": v(31.24, -72.02) * mm, "end": v(36.12, -82.98) * mm});
            skLineSegment(sketch, "E47.6.34.0", {"start": v(32.61, -71.4) * mm, "end": v(37.5, -82.37) * mm});
            skLineSegment(sketch, "E47.9.34.0", {"start": v(31.24, -72.02) * mm, "end": v(32.61, -71.4) * mm});
            skLineSegment(sketch, "E47.2.35.0", {"start": v(44.6, -78.75) * mm, "end": v(45.9, -78) * mm});
            skLineSegment(sketch, "E47.3.35.0", {"start": v(38.6, -68.36) * mm, "end": v(44.6, -78.75) * mm});
            skLineSegment(sketch, "E47.6.35.0", {"start": v(39.9, -67.6) * mm, "end": v(45.9, -78) * mm});
            skLineSegment(sketch, "E47.9.35.0", {"start": v(38.6, -68.36) * mm, "end": v(39.9, -67.6) * mm});
            skLineSegment(sketch, "E47.2.36.0", {"start": v(52.59, -73.66) * mm, "end": v(53.8, -72.78) * mm});
            skLineSegment(sketch, "E47.3.36.0", {"start": v(45.53, -63.95) * mm, "end": v(52.59, -73.66) * mm});
            skLineSegment(sketch, "E47.6.36.0", {"start": v(46.75, -63.07) * mm, "end": v(53.8, -72.78) * mm});
            skLineSegment(sketch, "E47.9.36.0", {"start": v(45.53, -63.95) * mm, "end": v(46.75, -63.07) * mm});
            skLineSegment(sketch, "E47.2.37.0", {"start": v(60, -67.76) * mm, "end": v(61.11, -66.75) * mm});
            skLineSegment(sketch, "E47.3.37.0", {"start": v(51.97, -58.84) * mm, "end": v(60, -67.76) * mm});
            skLineSegment(sketch, "E47.6.37.0", {"start": v(53.08, -57.84) * mm, "end": v(61.11, -66.75) * mm});
            skLineSegment(sketch, "E47.9.37.0", {"start": v(51.97, -58.84) * mm, "end": v(53.08, -57.84) * mm});
            skLineSegment(sketch, "E47.2.38.0", {"start": v(66.75, -61.11) * mm, "end": v(67.76, -60) * mm});
            skLineSegment(sketch, "E47.3.38.0", {"start": v(57.84, -53.08) * mm, "end": v(66.75, -61.11) * mm});
            skLineSegment(sketch, "E47.6.38.0", {"start": v(58.84, -51.97) * mm, "end": v(67.76, -60) * mm});
            skLineSegment(sketch, "E47.9.38.0", {"start": v(57.84, -53.08) * mm, "end": v(58.84, -51.97) * mm});
            skLineSegment(sketch, "E47.2.39.0", {"start": v(72.78, -53.8) * mm, "end": v(73.66, -52.59) * mm});
            skLineSegment(sketch, "E47.3.39.0", {"start": v(63.07, -46.75) * mm, "end": v(72.78, -53.8) * mm});
            skLineSegment(sketch, "E47.6.39.0", {"start": v(63.95, -45.53) * mm, "end": v(73.66, -52.59) * mm});
            skLineSegment(sketch, "E47.9.39.0", {"start": v(63.07, -46.75) * mm, "end": v(63.95, -45.53) * mm});
            skLineSegment(sketch, "E47.2.40.0", {"start": v(78, -45.9) * mm, "end": v(78.75, -44.6) * mm});
            skLineSegment(sketch, "E47.3.40.0", {"start": v(67.6, -39.9) * mm, "end": v(78, -45.9) * mm});
            skLineSegment(sketch, "E47.6.40.0", {"start": v(68.36, -38.6) * mm, "end": v(78.75, -44.6) * mm});
            skLineSegment(sketch, "E47.9.40.0", {"start": v(67.6, -39.9) * mm, "end": v(68.36, -38.6) * mm});
            skLineSegment(sketch, "E47.2.41.0", {"start": v(82.37, -37.5) * mm, "end": v(82.98, -36.12) * mm});
            skLineSegment(sketch, "E47.3.41.0", {"start": v(71.4, -32.61) * mm, "end": v(82.37, -37.5) * mm});
            skLineSegment(sketch, "E47.6.41.0", {"start": v(72.02, -31.24) * mm, "end": v(82.98, -36.12) * mm});
            skLineSegment(sketch, "E47.9.41.0", {"start": v(71.4, -32.61) * mm, "end": v(72.02, -31.24) * mm});
            skLineSegment(sketch, "E47.2.42.0", {"start": v(85.84, -28.68) * mm, "end": v(86.3, -27.25) * mm});
            skLineSegment(sketch, "E47.3.42.0", {"start": v(74.43, -24.97) * mm, "end": v(85.84, -28.68) * mm});
            skLineSegment(sketch, "E47.6.42.0", {"start": v(74.89, -23.54) * mm, "end": v(86.3, -27.25) * mm});
            skLineSegment(sketch, "E47.9.42.0", {"start": v(74.43, -24.97) * mm, "end": v(74.89, -23.54) * mm});
            skLineSegment(sketch, "E47.2.43.0", {"start": v(88.37, -19.55) * mm, "end": v(88.68, -18.08) * mm});
            skLineSegment(sketch, "E47.3.43.0", {"start": v(76.63, -17.05) * mm, "end": v(88.37, -19.55) * mm});
            skLineSegment(sketch, "E47.6.43.0", {"start": v(76.94, -15.59) * mm, "end": v(88.68, -18.08) * mm});
            skLineSegment(sketch, "E47.9.43.0", {"start": v(76.63, -17.05) * mm, "end": v(76.94, -15.59) * mm});
            skLineSegment(sketch, "E47.2.44.0", {"start": v(89.93, -10.2) * mm, "end": v(90.08, -8.71) * mm});
            skLineSegment(sketch, "E47.3.44.0", {"start": v(78, -8.95) * mm, "end": v(89.93, -10.2) * mm});
            skLineSegment(sketch, "E47.6.44.0", {"start": v(78.15, -7.46) * mm, "end": v(90.08, -8.71) * mm});
            skLineSegment(sketch, "E47.9.44.0", {"start": v(78, -8.95) * mm, "end": v(78.15, -7.46) * mm});
            skLineSegment(sketch, "E47.2.45.0", {"start": v(90.5, -0.75) * mm, "end": v(90.5, 0.75) * mm});
            skLineSegment(sketch, "E47.3.45.0", {"start": v(78.5, -0.75) * mm, "end": v(90.5, -0.75) * mm});
            skLineSegment(sketch, "E47.6.45.0", {"start": v(78.5, 0.75) * mm, "end": v(90.5, 0.75) * mm});
            skLineSegment(sketch, "E47.9.45.0", {"start": v(78.5, -0.75) * mm, "end": v(78.5, 0.75) * mm});
            skLineSegment(sketch, "E47.2.46.0", {"start": v(90.08, 8.71) * mm, "end": v(89.93, 10.2) * mm});
            skLineSegment(sketch, "E47.3.46.0", {"start": v(78.15, 7.46) * mm, "end": v(90.08, 8.71) * mm});
            skLineSegment(sketch, "E47.6.46.0", {"start": v(78, 8.95) * mm, "end": v(89.93, 10.2) * mm});
            skLineSegment(sketch, "E47.9.46.0", {"start": v(78.15, 7.46) * mm, "end": v(78, 8.95) * mm});
            skLineSegment(sketch, "E47.2.47.0", {"start": v(88.68, 18.08) * mm, "end": v(88.37, 19.55) * mm});
            skLineSegment(sketch, "E47.3.47.0", {"start": v(76.94, 15.59) * mm, "end": v(88.68, 18.08) * mm});
            skLineSegment(sketch, "E47.6.47.0", {"start": v(76.63, 17.05) * mm, "end": v(88.37, 19.55) * mm});
            skLineSegment(sketch, "E47.9.47.0", {"start": v(76.94, 15.59) * mm, "end": v(76.63, 17.05) * mm});
            skLineSegment(sketch, "E47.2.48.0", {"start": v(86.3, 27.25) * mm, "end": v(85.84, 28.68) * mm});
            skLineSegment(sketch, "E47.3.48.0", {"start": v(74.89, 23.54) * mm, "end": v(86.3, 27.25) * mm});
            skLineSegment(sketch, "E47.6.48.0", {"start": v(74.43, 24.97) * mm, "end": v(85.84, 28.68) * mm});
            skLineSegment(sketch, "E47.9.48.0", {"start": v(74.89, 23.54) * mm, "end": v(74.43, 24.97) * mm});
            skLineSegment(sketch, "E47.2.49.0", {"start": v(82.98, 36.12) * mm, "end": v(82.37, 37.5) * mm});
            skLineSegment(sketch, "E47.3.49.0", {"start": v(72.02, 31.24) * mm, "end": v(82.98, 36.12) * mm});
            skLineSegment(sketch, "E47.6.49.0", {"start": v(71.4, 32.61) * mm, "end": v(82.37, 37.5) * mm});
            skLineSegment(sketch, "E47.9.49.0", {"start": v(72.02, 31.24) * mm, "end": v(71.4, 32.61) * mm});
            skLineSegment(sketch, "E47.2.50.0", {"start": v(78.75, 44.6) * mm, "end": v(78, 45.9) * mm});
            skLineSegment(sketch, "E47.3.50.0", {"start": v(68.36, 38.6) * mm, "end": v(78.75, 44.6) * mm});
            skLineSegment(sketch, "E47.6.50.0", {"start": v(67.6, 39.9) * mm, "end": v(78, 45.9) * mm});
            skLineSegment(sketch, "E47.9.50.0", {"start": v(68.36, 38.6) * mm, "end": v(67.6, 39.9) * mm});
            skLineSegment(sketch, "E47.2.51.0", {"start": v(73.66, 52.59) * mm, "end": v(72.78, 53.8) * mm});
            skLineSegment(sketch, "E47.3.51.0", {"start": v(63.95, 45.53) * mm, "end": v(73.66, 52.59) * mm});
            skLineSegment(sketch, "E47.6.51.0", {"start": v(63.07, 46.75) * mm, "end": v(72.78, 53.8) * mm});
            skLineSegment(sketch, "E47.9.51.0", {"start": v(63.95, 45.53) * mm, "end": v(63.07, 46.75) * mm});
            skLineSegment(sketch, "E47.2.52.0", {"start": v(67.76, 60) * mm, "end": v(66.75, 61.11) * mm});
            skLineSegment(sketch, "E47.3.52.0", {"start": v(58.84, 51.97) * mm, "end": v(67.76, 60) * mm});
            skLineSegment(sketch, "E47.6.52.0", {"start": v(57.84, 53.08) * mm, "end": v(66.75, 61.11) * mm});
            skLineSegment(sketch, "E47.9.52.0", {"start": v(58.84, 51.97) * mm, "end": v(57.84, 53.08) * mm});
            skLineSegment(sketch, "E47.2.53.0", {"start": v(61.11, 66.75) * mm, "end": v(60, 67.76) * mm});
            skLineSegment(sketch, "E47.3.53.0", {"start": v(53.08, 57.84) * mm, "end": v(61.11, 66.75) * mm});
            skLineSegment(sketch, "E47.6.53.0", {"start": v(51.97, 58.84) * mm, "end": v(60, 67.76) * mm});
            skLineSegment(sketch, "E47.9.53.0", {"start": v(53.08, 57.84) * mm, "end": v(51.97, 58.84) * mm});
            skLineSegment(sketch, "E47.2.54.0", {"start": v(53.8, 72.78) * mm, "end": v(52.59, 73.66) * mm});
            skLineSegment(sketch, "E47.3.54.0", {"start": v(46.75, 63.07) * mm, "end": v(53.8, 72.78) * mm});
            skLineSegment(sketch, "E47.6.54.0", {"start": v(45.53, 63.95) * mm, "end": v(52.59, 73.66) * mm});
            skLineSegment(sketch, "E47.9.54.0", {"start": v(46.75, 63.07) * mm, "end": v(45.53, 63.95) * mm});
            skLineSegment(sketch, "E47.2.55.0", {"start": v(45.9, 78) * mm, "end": v(44.6, 78.75) * mm});
            skLineSegment(sketch, "E47.3.55.0", {"start": v(39.9, 67.6) * mm, "end": v(45.9, 78) * mm});
            skLineSegment(sketch, "E47.6.55.0", {"start": v(38.6, 68.36) * mm, "end": v(44.6, 78.75) * mm});
            skLineSegment(sketch, "E47.9.55.0", {"start": v(39.9, 67.6) * mm, "end": v(38.6, 68.36) * mm});
            skLineSegment(sketch, "E47.2.56.0", {"start": v(37.5, 82.37) * mm, "end": v(36.12, 82.98) * mm});
            skLineSegment(sketch, "E47.3.56.0", {"start": v(32.61, 71.4) * mm, "end": v(37.5, 82.37) * mm});
            skLineSegment(sketch, "E47.6.56.0", {"start": v(31.24, 72.02) * mm, "end": v(36.12, 82.98) * mm});
            skLineSegment(sketch, "E47.9.56.0", {"start": v(32.61, 71.4) * mm, "end": v(31.24, 72.02) * mm});
            skLineSegment(sketch, "E47.2.57.0", {"start": v(28.68, 85.84) * mm, "end": v(27.25, 86.3) * mm});
            skLineSegment(sketch, "E47.3.57.0", {"start": v(24.97, 74.43) * mm, "end": v(28.68, 85.84) * mm});
            skLineSegment(sketch, "E47.6.57.0", {"start": v(23.54, 74.89) * mm, "end": v(27.25, 86.3) * mm});
            skLineSegment(sketch, "E47.9.57.0", {"start": v(24.97, 74.43) * mm, "end": v(23.54, 74.89) * mm});
            skLineSegment(sketch, "E47.2.58.0", {"start": v(19.55, 88.37) * mm, "end": v(18.08, 88.68) * mm});
            skLineSegment(sketch, "E47.3.58.0", {"start": v(17.05, 76.63) * mm, "end": v(19.55, 88.37) * mm});
            skLineSegment(sketch, "E47.6.58.0", {"start": v(15.59, 76.94) * mm, "end": v(18.08, 88.68) * mm});
            skLineSegment(sketch, "E47.9.58.0", {"start": v(17.05, 76.63) * mm, "end": v(15.59, 76.94) * mm});
            skLineSegment(sketch, "E47.2.59.0", {"start": v(10.2, 89.93) * mm, "end": v(8.71, 90.08) * mm});
            skLineSegment(sketch, "E47.3.59.0", {"start": v(8.95, 78) * mm, "end": v(10.2, 89.93) * mm});
            skLineSegment(sketch, "E47.6.59.0", {"start": v(7.46, 78.15) * mm, "end": v(8.71, 90.08) * mm});
            skLineSegment(sketch, "E47.9.59.0", {"start": v(8.95, 78) * mm, "end": v(7.46, 78.15) * mm});
            skSolve(sketch);
        }
        {
            var Q0;
            Q0 = qSketchRegion(id + "F27", true);
            extrude(context, id + "F28", {"entities" : qUnion([Q0]), "operationType" : NewBodyOperationType.REMOVE, "oppositeDirection" : true, "depth" : 0.2 * mm, "offsetDistance" : 25 * mm});
        }
        {
            var Q0;
            Q0=makeQuery(id+"F26.boolean.opBoolean","COPY",FACE,{"derivedFrom":makeQuery(id+"F26.opExtrude","CAP_FACE",FACE,{"disambiguationData":[OSD([sQuery(id+"F25.wireOp",EDGE,"E42.bottom"),sQuery(id+"F25.wireOp",EDGE,"E42.top"),sQuery(id+"F25.wireOp",EDGE,"E42.left"),sQuery(id+"F25.wireOp",EDGE,"E42.right")])],"isStart":false})});
            extrude(context, id + "F29", {"entities" : qUnion([Q0]), "depth" : 1 * mm, "offsetDistance" : 25 * mm});
        }
        {
            var Q0;
            Q0=makeQuery(id+"F28.boolean.opBoolean","COPY",FACE,{"derivedFrom":makeQuery(id+"F28.opExtrude","CAP_FACE",FACE,{"disambiguationData":[OSD([sQuery(id+"F27.wireOp",EDGE,"E47.2.59.0"),sQuery(id+"F27.wireOp",EDGE,"E47.3.59.0"),sQuery(id+"F27.wireOp",EDGE,"E47.6.59.0"),sQuery(id+"F27.wireOp",EDGE,"E47.9.59.0")])],"isStart":false})});
            extrude(context, id + "F30", {"entities" : qUnion([Q0]), "depth" : 0.4 * mm, "offsetDistance" : 25 * mm});
        }
        {
            var Q0;
            Q0=makeQuery(id+"F15.opExtrude","CAP_FACE",FACE,{"disambiguationData":[OSD([sQuery(id+"F14.wireOp",EDGE,"E22.0.0"),sQuery(id+"F14.wireOp",EDGE,"E23"),sQuery(id+"F14.wireOp",EDGE,"E24"),sQuery(id+"F14.wireOp",EDGE,"E25"),sQuery(id+"F14.wireOp",EDGE,"E26.MirrorCS"),sQuery(id+"F14.wireOp",EDGE,"E27.MirrorCS"),sQuery(id+"F14.wireOp",EDGE,"E28.1.0"),sQuery(id+"F14.wireOp",EDGE,"E28.1.1"),sQuery(id+"F14.wireOp",EDGE,"E28.1.2"),sQuery(id+"F14.wireOp",EDGE,"E28.1.3"),sQuery(id+"F14.wireOp",EDGE,"E28.2.0"),sQuery(id+"F14.wireOp",EDGE,"E28.2.1"),sQuery(id+"F14.wireOp",EDGE,"E28.2.2"),sQuery(id+"F14.wireOp",EDGE,"E28.2.3"),sQuery(id+"F14.wireOp",EDGE,"E29.1.3.0"),sQuery(id+"F14.wireOp",EDGE,"E29.3.3.0"),sQuery(id+"F14.wireOp",EDGE,"E29.6.3.0"),sQuery(id+"F14.wireOp",EDGE,"E29.9.3.0"),sQuery(id+"F14.wireOp",EDGE,"E29.1.4.0"),sQuery(id+"F14.wireOp",EDGE,"E29.3.4.0"),sQuery(id+"F14.wireOp",EDGE,"E29.6.4.0"),sQuery(id+"F14.wireOp",EDGE,"E29.9.4.0"),sQuery(id+"F14.wireOp",EDGE,"E29.1.5.0"),sQuery(id+"F14.wireOp",EDGE,"E29.3.5.0"),sQuery(id+"F14.wireOp",EDGE,"E29.6.5.0"),sQuery(id+"F14.wireOp",EDGE,"E29.9.5.0"),sQuery(id+"F14.wireOp",EDGE,"E29.1.6.0"),sQuery(id+"F14.wireOp",EDGE,"E29.3.6.0"),sQuery(id+"F14.wireOp",EDGE,"E29.6.6.0"),sQuery(id+"F14.wireOp",EDGE,"E29.9.6.0"),sQuery(id+"F14.wireOp",EDGE,"E29.1.7.0"),sQuery(id+"F14.wireOp",EDGE,"E29.3.7.0"),sQuery(id+"F14.wireOp",EDGE,"E29.6.7.0"),sQuery(id+"F14.wireOp",EDGE,"E29.9.7.0"),sQuery(id+"F14.wireOp",EDGE,"E29.1.8.0"),sQuery(id+"F14.wireOp",EDGE,"E29.3.8.0"),sQuery(id+"F14.wireOp",EDGE,"E29.6.8.0"),sQuery(id+"F14.wireOp",EDGE,"E29.9.8.0"),sQuery(id+"F14.wireOp",EDGE,"E29.1.9.0"),sQuery(id+"F14.wireOp",EDGE,"E29.3.9.0"),sQuery(id+"F14.wireOp",EDGE,"E29.6.9.0"),sQuery(id+"F14.wireOp",EDGE,"E29.9.9.0"),sQuery(id+"F14.wireOp",EDGE,"E29.1.10.0"),sQuery(id+"F14.wireOp",EDGE,"E29.3.10.0"),sQuery(id+"F14.wireOp",EDGE,"E29.6.10.0"),sQuery(id+"F14.wireOp",EDGE,"E29.9.10.0"),sQuery(id+"F14.wireOp",EDGE,"E29.1.11.0"),sQuery(id+"F14.wireOp",EDGE,"E29.3.11.0"),sQuery(id+"F14.wireOp",EDGE,"E29.6.11.0"),sQuery(id+"F14.wireOp",EDGE,"E29.9.11.0"),sQuery(id+"F14.wireOp",EDGE,"E29.1.12.0"),sQuery(id+"F14.wireOp",EDGE,"E29.3.12.0"),sQuery(id+"F14.wireOp",EDGE,"E29.6.12.0"),sQuery(id+"F14.wireOp",EDGE,"E29.9.12.0"),sQuery(id+"F14.wireOp",EDGE,"E29.1.13.0"),sQuery(id+"F14.wireOp",EDGE,"E29.3.13.0"),sQuery(id+"F14.wireOp",EDGE,"E29.6.13.0"),sQuery(id+"F14.wireOp",EDGE,"E29.9.13.0"),sQuery(id+"F14.wireOp",EDGE,"E29.1.14.0"),sQuery(id+"F14.wireOp",EDGE,"E29.3.14.0"),sQuery(id+"F14.wireOp",EDGE,"E29.6.14.0"),sQuery(id+"F14.wireOp",EDGE,"E29.9.14.0"),sQuery(id+"F14.wireOp",EDGE,"E29.1.15.0"),sQuery(id+"F14.wireOp",EDGE,"E29.3.15.0"),sQuery(id+"F14.wireOp",EDGE,"E29.6.15.0"),sQuery(id+"F14.wireOp",EDGE,"E29.9.15.0"),sQuery(id+"F14.wireOp",EDGE,"E29.1.16.0"),sQuery(id+"F14.wireOp",EDGE,"E29.3.16.0"),sQuery(id+"F14.wireOp",EDGE,"E29.6.16.0"),sQuery(id+"F14.wireOp",EDGE,"E29.9.16.0"),sQuery(id+"F14.wireOp",EDGE,"E29.1.17.0"),sQuery(id+"F14.wireOp",EDGE,"E29.3.17.0"),sQuery(id+"F14.wireOp",EDGE,"E29.6.17.0"),sQuery(id+"F14.wireOp",EDGE,"E29.9.17.0"),sQuery(id+"F14.wireOp",EDGE,"E29.1.18.0"),sQuery(id+"F14.wireOp",EDGE,"E29.3.18.0"),sQuery(id+"F14.wireOp",EDGE,"E29.6.18.0"),sQuery(id+"F14.wireOp",EDGE,"E29.9.18.0"),sQuery(id+"F14.wireOp",EDGE,"E29.1.19.0"),sQuery(id+"F14.wireOp",EDGE,"E29.3.19.0"),sQuery(id+"F14.wireOp",EDGE,"E29.6.19.0"),sQuery(id+"F14.wireOp",EDGE,"E29.9.19.0"),sQuery(id+"F14.wireOp",EDGE,"E29.1.20.0"),sQuery(id+"F14.wireOp",EDGE,"E29.3.20.0"),sQuery(id+"F14.wireOp",EDGE,"E29.6.20.0"),sQuery(id+"F14.wireOp",EDGE,"E29.9.20.0"),sQuery(id+"F14.wireOp",EDGE,"E29.1.21.0"),sQuery(id+"F14.wireOp",EDGE,"E29.3.21.0"),sQuery(id+"F14.wireOp",EDGE,"E29.6.21.0"),sQuery(id+"F14.wireOp",EDGE,"E29.9.21.0"),sQuery(id+"F14.wireOp",EDGE,"E29.1.22.0"),sQuery(id+"F14.wireOp",EDGE,"E29.3.22.0"),sQuery(id+"F14.wireOp",EDGE,"E29.6.22.0"),sQuery(id+"F14.wireOp",EDGE,"E29.9.22.0"),sQuery(id+"F14.wireOp",EDGE,"E29.1.23.0"),sQuery(id+"F14.wireOp",EDGE,"E29.3.23.0"),sQuery(id+"F14.wireOp",EDGE,"E29.6.23.0"),sQuery(id+"F14.wireOp",EDGE,"E29.9.23.0"),sQuery(id+"F14.wireOp",EDGE,"E29.1.24.0"),sQuery(id+"F14.wireOp",EDGE,"E29.3.24.0"),sQuery(id+"F14.wireOp",EDGE,"E29.6.24.0"),sQuery(id+"F14.wireOp",EDGE,"E29.9.24.0"),sQuery(id+"F14.wireOp",EDGE,"E29.1.25.0"),sQuery(id+"F14.wireOp",EDGE,"E29.3.25.0"),sQuery(id+"F14.wireOp",EDGE,"E29.6.25.0"),sQuery(id+"F14.wireOp",EDGE,"E29.9.25.0"),sQuery(id+"F14.wireOp",EDGE,"E29.1.26.0"),sQuery(id+"F14.wireOp",EDGE,"E29.3.26.0"),sQuery(id+"F14.wireOp",EDGE,"E29.6.26.0"),sQuery(id+"F14.wireOp",EDGE,"E29.9.26.0"),sQuery(id+"F14.wireOp",EDGE,"E29.1.27.0"),sQuery(id+"F14.wireOp",EDGE,"E29.3.27.0"),sQuery(id+"F14.wireOp",EDGE,"E29.6.27.0"),sQuery(id+"F14.wireOp",EDGE,"E29.9.27.0"),sQuery(id+"F14.wireOp",EDGE,"E29.1.28.0"),sQuery(id+"F14.wireOp",EDGE,"E29.3.28.0"),sQuery(id+"F14.wireOp",EDGE,"E29.6.28.0"),sQuery(id+"F14.wireOp",EDGE,"E29.9.28.0"),sQuery(id+"F14.wireOp",EDGE,"E29.1.29.0"),sQuery(id+"F14.wireOp",EDGE,"E29.3.29.0"),sQuery(id+"F14.wireOp",EDGE,"E29.6.29.0"),sQuery(id+"F14.wireOp",EDGE,"E29.9.29.0"),sQuery(id+"F14.wireOp",EDGE,"E29.1.30.0"),sQuery(id+"F14.wireOp",EDGE,"E29.3.30.0"),sQuery(id+"F14.wireOp",EDGE,"E29.6.30.0"),sQuery(id+"F14.wireOp",EDGE,"E29.9.30.0"),sQuery(id+"F14.wireOp",EDGE,"E29.1.31.0"),sQuery(id+"F14.wireOp",EDGE,"E29.3.31.0"),sQuery(id+"F14.wireOp",EDGE,"E29.6.31.0"),sQuery(id+"F14.wireOp",EDGE,"E29.9.31.0"),sQuery(id+"F14.wireOp",EDGE,"E29.1.32.0"),sQuery(id+"F14.wireOp",EDGE,"E29.3.32.0"),sQuery(id+"F14.wireOp",EDGE,"E29.6.32.0"),sQuery(id+"F14.wireOp",EDGE,"E29.9.32.0"),sQuery(id+"F14.wireOp",EDGE,"E29.1.33.0"),sQuery(id+"F14.wireOp",EDGE,"E29.3.33.0"),sQuery(id+"F14.wireOp",EDGE,"E29.6.33.0"),sQuery(id+"F14.wireOp",EDGE,"E29.9.33.0"),sQuery(id+"F14.wireOp",EDGE,"E29.1.34.0"),sQuery(id+"F14.wireOp",EDGE,"E29.3.34.0"),sQuery(id+"F14.wireOp",EDGE,"E29.6.34.0"),sQuery(id+"F14.wireOp",EDGE,"E29.9.34.0"),sQuery(id+"F14.wireOp",EDGE,"E29.1.35.0"),sQuery(id+"F14.wireOp",EDGE,"E29.3.35.0"),sQuery(id+"F14.wireOp",EDGE,"E29.6.35.0"),sQuery(id+"F14.wireOp",EDGE,"E29.9.35.0"),sQuery(id+"F14.wireOp",EDGE,"E29.1.36.0"),sQuery(id+"F14.wireOp",EDGE,"E29.3.36.0"),sQuery(id+"F14.wireOp",EDGE,"E29.6.36.0"),sQuery(id+"F14.wireOp",EDGE,"E29.9.36.0"),sQuery(id+"F14.wireOp",EDGE,"E29.1.37.0"),sQuery(id+"F14.wireOp",EDGE,"E29.3.37.0"),sQuery(id+"F14.wireOp",EDGE,"E29.6.37.0"),sQuery(id+"F14.wireOp",EDGE,"E29.9.37.0"),sQuery(id+"F14.wireOp",EDGE,"E29.1.38.0"),sQuery(id+"F14.wireOp",EDGE,"E29.3.38.0"),sQuery(id+"F14.wireOp",EDGE,"E29.6.38.0"),sQuery(id+"F14.wireOp",EDGE,"E29.9.38.0"),sQuery(id+"F14.wireOp",EDGE,"E29.1.39.0"),sQuery(id+"F14.wireOp",EDGE,"E29.3.39.0"),sQuery(id+"F14.wireOp",EDGE,"E29.6.39.0"),sQuery(id+"F14.wireOp",EDGE,"E29.9.39.0")])],"isStart":false});
            var sketch = newSketch(context, id + "F31", { "sketchPlane" : qUnion([Q0])});
            skCircle(sketch, "E48.0", {"center": v(0, 0) * mm, "radius": 3 * mm});
            skCircle(sketch, "E49.0", {"center": v(0, 0) * mm, "radius": 5 * mm});
            skSolve(sketch);
        }
        {
            var Q0;
            Q0 = qSketchRegion(id + "F31", true);
            extrude(context, id + "F32", {"entities" : qUnion([Q0]), "operationType" : NewBodyOperationType.ADD, "depth" : 5 * mm, "offsetDistance" : 25 * mm});
        }
        {
            var Q0;
            Q0=makeQuery(id+"F32.opExtrude","CAP_FACE",FACE,{"disambiguationData":[OSD([sQuery(id+"F31.wireOp",EDGE,"E48.0"),sQuery(id+"F31.wireOp",EDGE,"E49.0")])],"isStart":false});
            var sketch = newSketch(context, id + "F33", { "sketchPlane" : qUnion([Q0])});
            skLineSegment(sketch, "E50", {"start": v(0, 50) * mm, "end": v(1.5, 50) * mm});
            skLineSegment(sketch, "E51", {"start": v(1.5, 50) * mm, "end": v(3, 4) * mm});
            skLineSegment(sketch, "E52.MirrorCS", {"start": v(0, 50) * mm, "end": v(-1.5, 50) * mm});
            skLineSegment(sketch, "E53.MirrorCS", {"start": v(-1.5, 50) * mm, "end": v(-3, 4) * mm});
            skCircle(sketch, "E54.0", {"center": v(0, 0) * mm, "radius": 3 * mm});
            skCircle(sketch, "E55.0", {"center": v(0, 0) * mm, "radius": 5 * mm});
            skSolve(sketch);
        }
        {
            var Q0;
            Q0 = qSketchRegion(id + "F33", true);
            extrude(context, id + "F34", {"entities" : qUnion([Q0]), "operationType" : NewBodyOperationType.ADD, "depth" : 1 * mm, "offsetDistance" : 25 * mm});
        }
        {
            var Q0;
            Q0=makeQuery(id+"F6.opExtrude","CAP_FACE",FACE,{"disambiguationData":[OSD([sQuery(id+"F0.wireOp",EDGE,"E0")])],"isStart":false});
            var sketch = newSketch(context, id + "F35", { "sketchPlane" : qUnion([Q0])});
            skCircle(sketch, "E56", {"center": v(0, 0) * mm, "radius": 5 * mm});
            skLineSegment(sketch, "E57", {"start": v(0, 80) * mm, "end": v(0.5, 80) * mm});
            skLineSegment(sketch, "E58", {"start": v(0.5, 80) * mm, "end": v(2, 4.58) * mm});
            skLineSegment(sketch, "E59.MirrorCS", {"start": v(0, 80) * mm, "end": v(-0.5, 80) * mm});
            skLineSegment(sketch, "E60.MirrorCS", {"start": v(-0.5, 80) * mm, "end": v(-2, 4.58) * mm});
            skSolve(sketch);
        }
        {
            var Q0;
            Q0 = qSketchRegion(id + "F35", true);
            extrude(context, id + "F36", {"entities" : qUnion([Q0]), "operationType" : NewBodyOperationType.ADD, "oppositeDirection" : true, "depth" : 1 * mm, "offsetDistance" : 25 * mm});
        }
    });
